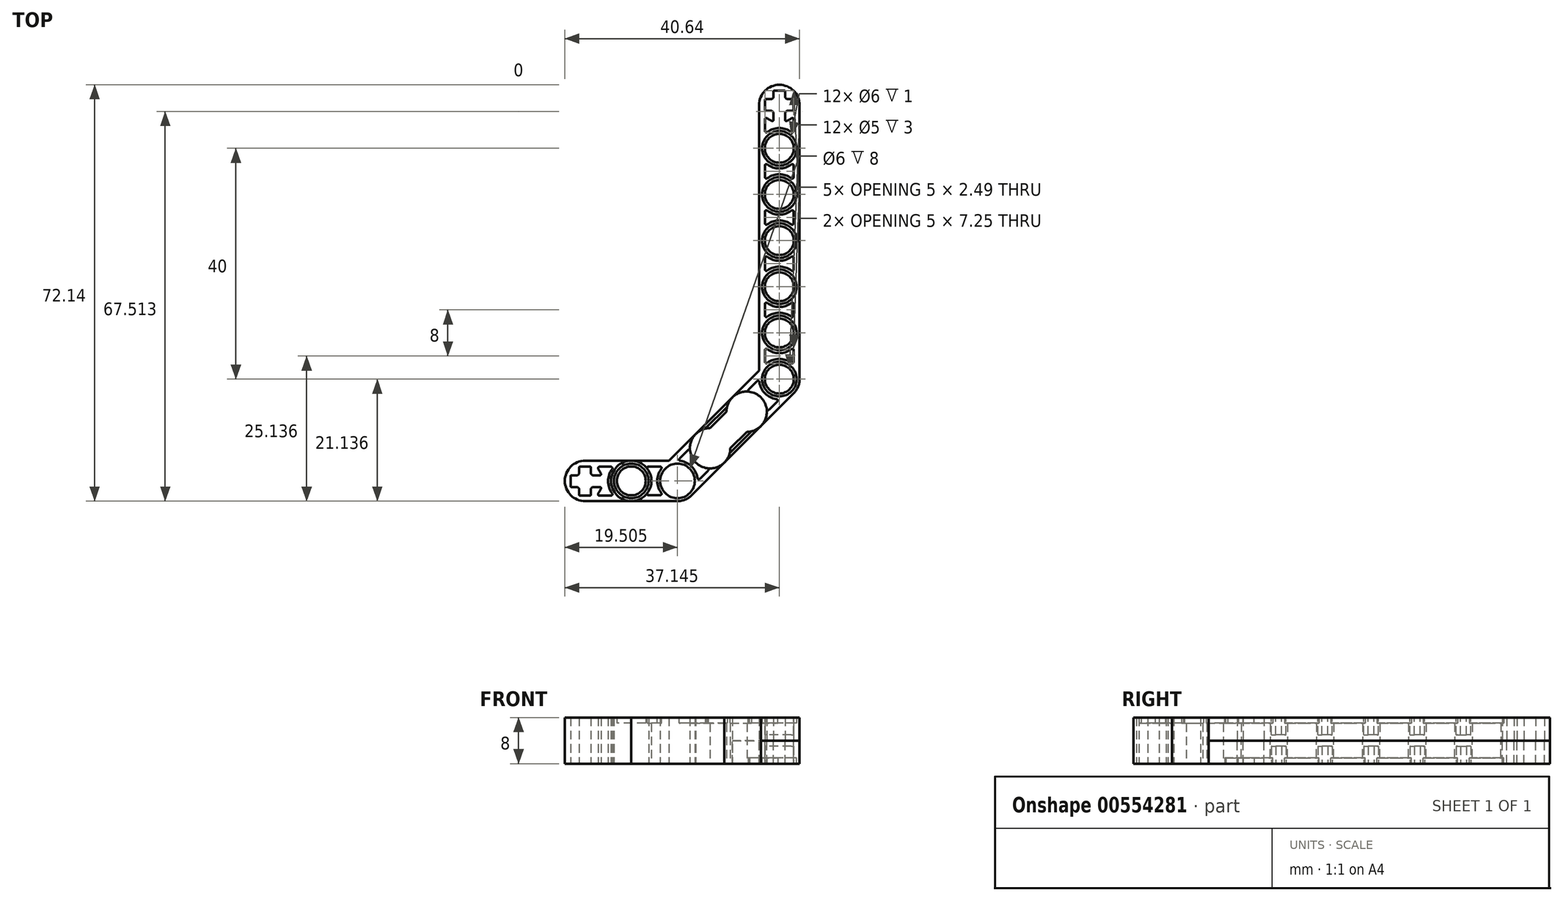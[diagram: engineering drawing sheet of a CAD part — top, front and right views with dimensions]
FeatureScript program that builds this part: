
annotation { "Feature Type Name" : "Feature", "Feature Type Description" : "" }
export const myFeature = defineFeature(function(context is Context, id is Id, definition is map)
    precondition{}
    {
        {
            var Q0;
            Q0=qCreatedBy(makeId("Top.planeOp"),FACE);
            var sketch = newSketch(context, id + "F0", { "sketchPlane" : qUnion([Q0])});
            skArc(sketch, "E0", {"start": v(42.78, 53.86) * mm, "mid": v(39.28, 57.36) * mm, "end": v(35.78, 53.86) * mm});
            skCircle(sketch, "E1", {"center": v(39.28, 6.36) * mm, "radius": 3.5 * mm});
            skLineSegment(sketch, "E2", {"start": v(35.78, 53.86) * mm, "end": v(35.78, 6.36) * mm});
            skLineSegment(sketch, "E3", {"start": v(42.78, 53.86) * mm, "end": v(42.78, 6.36) * mm});
            skCircle(sketch, "E4", {"center": v(39.28, 6.36) * mm, "radius": 2.5 * mm});
            skCircle(sketch, "E5", {"center": v(39.28, 6.36) * mm, "radius": 3 * mm});
            skCircle(sketch, "E6", {"center": v(21.64, -11.28) * mm, "radius": 3.5 * mm});
            skLineSegment(sketch, "E7", {"start": v(21.64, -11.28) * mm, "end": v(5.64, -11.28) * mm});
            skCircle(sketch, "E8", {"center": v(5.64, -11.28) * mm, "radius": 3.5 * mm});
            skLineSegment(sketch, "E9", {"start": v(21.64, -7.78) * mm, "end": v(5.64, -7.78) * mm});
            skLineSegment(sketch, "E10", {"start": v(21.64, -14.78) * mm, "end": v(5.64, -14.78) * mm});
            skLineSegment(sketch, "E11", {"start": v(41.76, 3.88) * mm, "end": v(24.12, -13.76) * mm});
            skLineSegment(sketch, "E12", {"start": v(39.28, 6.36) * mm, "end": v(39.28, 14.36) * mm});
            skLineSegment(sketch, "E13", {"start": v(39.28, 14.36) * mm, "end": v(39.28, 22.36) * mm});
            skLineSegment(sketch, "E14", {"start": v(39.28, 22.36) * mm, "end": v(39.28, 30.36) * mm});
            skLineSegment(sketch, "E15", {"start": v(39.28, 30.36) * mm, "end": v(39.28, 38.36) * mm});
            skLineSegment(sketch, "E16", {"start": v(39.28, 38.36) * mm, "end": v(39.28, 46.36) * mm});
            skCircle(sketch, "E17", {"center": v(39.28, 14.36) * mm, "radius": 2.5 * mm});
            skCircle(sketch, "E18", {"center": v(39.28, 14.36) * mm, "radius": 3 * mm});
            skCircle(sketch, "E19", {"center": v(39.28, 14.36) * mm, "radius": 3.5 * mm});
            skCircle(sketch, "E20", {"center": v(39.28, 22.36) * mm, "radius": 2.5 * mm});
            skCircle(sketch, "E21", {"center": v(39.28, 22.36) * mm, "radius": 3 * mm});
            skCircle(sketch, "E22", {"center": v(39.28, 22.36) * mm, "radius": 3.5 * mm});
            skCircle(sketch, "E23", {"center": v(39.28, 30.36) * mm, "radius": 2.5 * mm});
            skCircle(sketch, "E24", {"center": v(39.28, 30.36) * mm, "radius": 3 * mm});
            skCircle(sketch, "E25", {"center": v(39.28, 30.36) * mm, "radius": 3.5 * mm});
            skCircle(sketch, "E26", {"center": v(39.28, 38.36) * mm, "radius": 2.5 * mm});
            skCircle(sketch, "E27", {"center": v(39.28, 38.36) * mm, "radius": 3 * mm});
            skCircle(sketch, "E28", {"center": v(39.28, 38.36) * mm, "radius": 3.5 * mm});
            skCircle(sketch, "E29", {"center": v(39.28, 46.36) * mm, "radius": 2.5 * mm});
            skCircle(sketch, "E30", {"center": v(39.28, 46.36) * mm, "radius": 3 * mm});
            skArc(sketch, "E31", {"start": v(35.78, 46.36) * mm, "mid": v(39.28, 42.86) * mm, "end": v(42.78, 46.36) * mm});
            skLineSegment(sketch, "E32", {"start": v(39.28, 56.36) * mm, "end": v(38.4, 56.36) * mm});
            skLineSegment(sketch, "E33", {"start": v(39.28, 56.36) * mm, "end": v(40.16, 56.36) * mm});
            skLineSegment(sketch, "E34", {"start": v(41.78, 53.86) * mm, "end": v(41.78, 54.74) * mm});
            skLineSegment(sketch, "E35", {"start": v(41.78, 53.86) * mm, "end": v(41.78, 52.98) * mm});
            skLineSegment(sketch, "E36", {"start": v(36.78, 53.86) * mm, "end": v(36.78, 54.74) * mm});
            skLineSegment(sketch, "E37", {"start": v(36.78, 53.86) * mm, "end": v(36.78, 52.98) * mm});
            skLineSegment(sketch, "E38", {"start": v(36.9, 54.86) * mm, "end": v(37.78, 54.86) * mm});
            skLineSegment(sketch, "E39", {"start": v(38.28, 55.36) * mm, "end": v(38.28, 56.24) * mm});
            skLineSegment(sketch, "E40", {"start": v(40.28, 56.24) * mm, "end": v(40.28, 55.36) * mm});
            skLineSegment(sketch, "E41", {"start": v(40.78, 54.86) * mm, "end": v(41.66, 54.86) * mm});
            skLineSegment(sketch, "E42", {"start": v(41.66, 52.86) * mm, "end": v(40.78, 52.86) * mm});
            skLineSegment(sketch, "E43", {"start": v(36.9, 52.86) * mm, "end": v(37.78, 52.86) * mm});
            skPoint(sketch, "E44.visualSharp", {"position": v(38.28, 56.36) * mm});
            skArc(sketch, "E44.filletArc", {"start": v(38.4, 56.36) * mm, "mid": v(38.32, 56.32) * mm, "end": v(38.28, 56.24) * mm});
            skPoint(sketch, "E45.visualSharp", {"position": v(40.28, 56.36) * mm});
            skArc(sketch, "E45.filletArc", {"start": v(40.28, 56.24) * mm, "mid": v(40.25, 56.32) * mm, "end": v(40.16, 56.36) * mm});
            skPoint(sketch, "E46.visualSharp", {"position": v(36.78, 54.86) * mm});
            skArc(sketch, "E46.filletArc", {"start": v(36.9, 54.86) * mm, "mid": v(36.82, 54.82) * mm, "end": v(36.78, 54.74) * mm});
            skPoint(sketch, "E47.visualSharp", {"position": v(36.78, 52.86) * mm});
            skArc(sketch, "E47.filletArc", {"start": v(36.78, 52.98) * mm, "mid": v(36.82, 52.9) * mm, "end": v(36.9, 52.86) * mm});
            skPoint(sketch, "E48.visualSharp", {"position": v(41.78, 54.86) * mm});
            skArc(sketch, "E48.filletArc", {"start": v(41.78, 54.74) * mm, "mid": v(41.75, 54.82) * mm, "end": v(41.66, 54.86) * mm});
            skPoint(sketch, "E49.visualSharp", {"position": v(41.78, 52.86) * mm});
            skArc(sketch, "E49.filletArc", {"start": v(41.66, 52.86) * mm, "mid": v(41.75, 52.9) * mm, "end": v(41.78, 52.98) * mm});
            skPoint(sketch, "E50.visualSharp", {"position": v(38.28, 54.86) * mm});
            skArc(sketch, "E50.filletArc", {"start": v(37.78, 54.86) * mm, "mid": v(38.14, 55) * mm, "end": v(38.28, 55.36) * mm});
            skPoint(sketch, "E51.visualSharp", {"position": v(40.28, 54.86) * mm});
            skArc(sketch, "E51.filletArc", {"start": v(40.28, 55.36) * mm, "mid": v(40.43, 55) * mm, "end": v(40.78, 54.86) * mm});
            skLineSegment(sketch, "E52", {"start": v(36.78, 50.1) * mm, "end": v(36.78, 49.36) * mm});
            skLineSegment(sketch, "E53", {"start": v(36.78, 50.1) * mm, "end": v(36.78, 51.35) * mm});
            skLineSegment(sketch, "E54", {"start": v(41.78, 50.04) * mm, "end": v(41.78, 49.36) * mm});
            skLineSegment(sketch, "E55", {"start": v(41.78, 50.04) * mm, "end": v(41.78, 51.35) * mm});
            skArc(sketch, "E56", {"start": v(37.19, 51.55) * mm, "mid": v(37.59, 51.3) * mm, "end": v(38.01, 51.1) * mm});
            skLineSegment(sketch, "E57.trimOffspring", {"start": v(39.28, 49.36) * mm, "end": v(39.28, 6.36) * mm});
            skLineSegment(sketch, "E58", {"start": v(40.28, 52.36) * mm, "end": v(40.28, 51.28) * mm});
            skLineSegment(sketch, "E59", {"start": v(38.28, 52.36) * mm, "end": v(38.28, 51.28) * mm});
            skPoint(sketch, "E60.visualSharp", {"position": v(38.28, 52.86) * mm});
            skArc(sketch, "E60.filletArc", {"start": v(38.28, 52.36) * mm, "mid": v(38.14, 52.7) * mm, "end": v(37.78, 52.86) * mm});
            skPoint(sketch, "E61.visualSharp", {"position": v(40.28, 52.86) * mm});
            skArc(sketch, "E61.filletArc", {"start": v(40.78, 52.86) * mm, "mid": v(40.43, 52.7) * mm, "end": v(40.28, 52.36) * mm});
            skArc(sketch, "E62.trimOffspring", {"start": v(40.56, 51.1) * mm, "mid": v(40.98, 51.3) * mm, "end": v(41.38, 51.55) * mm});
            skPoint(sketch, "E63.visualSharp", {"position": v(40.28, 51) * mm});
            skArc(sketch, "E63.filletArc", {"start": v(40.28, 51.28) * mm, "mid": v(40.37, 51.12) * mm, "end": v(40.56, 51.1) * mm});
            skPoint(sketch, "E64.visualSharp", {"position": v(38.28, 51) * mm});
            skArc(sketch, "E64.filletArc", {"start": v(38.01, 51.1) * mm, "mid": v(38.2, 51.12) * mm, "end": v(38.28, 51.28) * mm});
            skPoint(sketch, "E65.visualSharp", {"position": v(36.78, 51.9) * mm});
            skArc(sketch, "E65.filletArc", {"start": v(37.19, 51.55) * mm, "mid": v(36.92, 51.58) * mm, "end": v(36.78, 51.35) * mm});
            skArc(sketch, "E66.trimOffspring", {"start": v(41.38, 49.16) * mm, "mid": v(39.28, 49.86) * mm, "end": v(37.19, 49.16) * mm});
            skPoint(sketch, "E67.visualSharp", {"position": v(36.78, 48.8) * mm});
            skArc(sketch, "E67.filletArc", {"start": v(36.78, 49.36) * mm, "mid": v(36.92, 49.14) * mm, "end": v(37.19, 49.16) * mm});
            skPoint(sketch, "E68.visualSharp", {"position": v(41.78, 48.8) * mm});
            skArc(sketch, "E68.filletArc", {"start": v(41.38, 49.16) * mm, "mid": v(41.64, 49.14) * mm, "end": v(41.78, 49.36) * mm});
            skPoint(sketch, "E69.visualSharp", {"position": v(41.78, 51.9) * mm});
            skArc(sketch, "E69.filletArc", {"start": v(41.78, 51.35) * mm, "mid": v(41.64, 51.58) * mm, "end": v(41.38, 51.55) * mm});
            skLineSegment(sketch, "E70", {"start": v(3.13, -11.33) * mm, "end": v(3.13, -12.21) * mm});
            skLineSegment(sketch, "E71", {"start": v(3.13, -11.33) * mm, "end": v(3.13, -10.45) * mm});
            skLineSegment(sketch, "E72", {"start": v(5.63, -8.83) * mm, "end": v(4.75, -8.83) * mm});
            skLineSegment(sketch, "E73", {"start": v(5.63, -8.83) * mm, "end": v(6.51, -8.83) * mm});
            skLineSegment(sketch, "E74", {"start": v(5.63, -13.83) * mm, "end": v(4.75, -13.83) * mm});
            skLineSegment(sketch, "E75", {"start": v(5.63, -13.83) * mm, "end": v(6.51, -13.83) * mm});
            skLineSegment(sketch, "E76", {"start": v(4.63, -13.71) * mm, "end": v(4.63, -12.83) * mm});
            skLineSegment(sketch, "E77", {"start": v(4.13, -12.33) * mm, "end": v(3.25, -12.33) * mm});
            skLineSegment(sketch, "E78", {"start": v(3.25, -10.33) * mm, "end": v(4.13, -10.33) * mm});
            skLineSegment(sketch, "E79", {"start": v(4.63, -9.83) * mm, "end": v(4.63, -8.95) * mm});
            skLineSegment(sketch, "E80", {"start": v(6.63, -8.95) * mm, "end": v(6.63, -9.83) * mm});
            skLineSegment(sketch, "E81", {"start": v(6.63, -13.71) * mm, "end": v(6.63, -12.83) * mm});
            skPoint(sketch, "E82.visualSharp", {"position": v(3.13, -12.33) * mm});
            skArc(sketch, "E82.filletArc", {"start": v(3.13, -12.21) * mm, "mid": v(3.17, -12.3) * mm, "end": v(3.25, -12.33) * mm});
            skPoint(sketch, "E83.visualSharp", {"position": v(3.13, -10.33) * mm});
            skArc(sketch, "E83.filletArc", {"start": v(3.25, -10.33) * mm, "mid": v(3.17, -10.37) * mm, "end": v(3.13, -10.45) * mm});
            skPoint(sketch, "E84.visualSharp", {"position": v(4.63, -13.83) * mm});
            skArc(sketch, "E84.filletArc", {"start": v(4.63, -13.71) * mm, "mid": v(4.67, -13.8) * mm, "end": v(4.75, -13.83) * mm});
            skPoint(sketch, "E85.visualSharp", {"position": v(6.63, -13.83) * mm});
            skArc(sketch, "E85.filletArc", {"start": v(6.51, -13.83) * mm, "mid": v(6.6, -13.8) * mm, "end": v(6.63, -13.71) * mm});
            skPoint(sketch, "E86.visualSharp", {"position": v(4.63, -8.83) * mm});
            skArc(sketch, "E86.filletArc", {"start": v(4.75, -8.83) * mm, "mid": v(4.67, -8.87) * mm, "end": v(4.63, -8.95) * mm});
            skPoint(sketch, "E87.visualSharp", {"position": v(6.63, -8.83) * mm});
            skArc(sketch, "E87.filletArc", {"start": v(6.63, -8.95) * mm, "mid": v(6.6, -8.87) * mm, "end": v(6.51, -8.83) * mm});
            skPoint(sketch, "E88.visualSharp", {"position": v(4.63, -12.33) * mm});
            skArc(sketch, "E88.filletArc", {"start": v(4.63, -12.83) * mm, "mid": v(4.48, -12.48) * mm, "end": v(4.13, -12.33) * mm});
            skPoint(sketch, "E89.visualSharp", {"position": v(4.63, -10.33) * mm});
            skArc(sketch, "E89.filletArc", {"start": v(4.13, -10.33) * mm, "mid": v(4.48, -10.19) * mm, "end": v(4.63, -9.83) * mm});
            skLineSegment(sketch, "E90", {"start": v(9.39, -13.83) * mm, "end": v(10.13, -13.83) * mm});
            skLineSegment(sketch, "E91", {"start": v(9.39, -13.83) * mm, "end": v(8.14, -13.83) * mm});
            skLineSegment(sketch, "E92", {"start": v(9.45, -8.83) * mm, "end": v(10.13, -8.83) * mm});
            skLineSegment(sketch, "E93", {"start": v(9.45, -8.83) * mm, "end": v(8.14, -8.83) * mm});
            skArc(sketch, "E94", {"start": v(7.93, -13.43) * mm, "mid": v(8.2, -13.03) * mm, "end": v(8.4, -12.6) * mm});
            skLineSegment(sketch, "E95", {"start": v(7.13, -10.33) * mm, "end": v(8.2, -10.33) * mm});
            skLineSegment(sketch, "E96", {"start": v(7.13, -12.33) * mm, "end": v(8.2, -12.33) * mm});
            skPoint(sketch, "E97.visualSharp", {"position": v(6.63, -12.33) * mm});
            skArc(sketch, "E97.filletArc", {"start": v(7.13, -12.33) * mm, "mid": v(6.78, -12.48) * mm, "end": v(6.63, -12.83) * mm});
            skPoint(sketch, "E98.visualSharp", {"position": v(6.63, -10.33) * mm});
            skArc(sketch, "E98.filletArc", {"start": v(6.63, -9.83) * mm, "mid": v(6.78, -10.19) * mm, "end": v(7.13, -10.33) * mm});
            skArc(sketch, "E99.trimOffspring", {"start": v(8.4, -10.06) * mm, "mid": v(8.2, -9.63) * mm, "end": v(7.93, -9.24) * mm});
            skPoint(sketch, "E100.visualSharp", {"position": v(8.49, -10.33) * mm});
            skArc(sketch, "E100.filletArc", {"start": v(8.2, -10.33) * mm, "mid": v(8.37, -10.25) * mm, "end": v(8.4, -10.06) * mm});
            skPoint(sketch, "E101.visualSharp", {"position": v(8.49, -12.33) * mm});
            skArc(sketch, "E101.filletArc", {"start": v(8.4, -12.6) * mm, "mid": v(8.37, -12.42) * mm, "end": v(8.2, -12.33) * mm});
            skPoint(sketch, "E102.visualSharp", {"position": v(7.58, -13.83) * mm});
            skArc(sketch, "E102.filletArc", {"start": v(7.93, -13.43) * mm, "mid": v(7.91, -13.7) * mm, "end": v(8.14, -13.83) * mm});
            skArc(sketch, "E103.trimOffspring", {"start": v(10.33, -9.24) * mm, "mid": v(9.63, -11.33) * mm, "end": v(10.33, -13.43) * mm});
            skPoint(sketch, "E104.visualSharp", {"position": v(10.68, -13.83) * mm});
            skArc(sketch, "E104.filletArc", {"start": v(10.13, -13.83) * mm, "mid": v(10.35, -13.7) * mm, "end": v(10.33, -13.43) * mm});
            skPoint(sketch, "E105.visualSharp", {"position": v(10.68, -8.83) * mm});
            skArc(sketch, "E105.filletArc", {"start": v(10.33, -9.24) * mm, "mid": v(10.35, -8.97) * mm, "end": v(10.13, -8.83) * mm});
            skPoint(sketch, "E106.visualSharp", {"position": v(7.58, -8.83) * mm});
            skArc(sketch, "E106.filletArc", {"start": v(8.14, -8.83) * mm, "mid": v(7.91, -8.97) * mm, "end": v(7.93, -9.24) * mm});
            skLineSegment(sketch, "E107", {"start": v(21.64, -11.28) * mm, "end": v(39.28, 6.36) * mm});
            skLineSegment(sketch, "E108", {"start": v(21.64, -11.28) * mm, "end": v(13.64, -11.28) * mm});
            skCircle(sketch, "E109", {"center": v(13.64, -11.28) * mm, "radius": 3.5 * mm});
            skCircle(sketch, "E110", {"center": v(13.64, -11.28) * mm, "radius": 3 * mm});
            skCircle(sketch, "E111", {"center": v(13.64, -11.28) * mm, "radius": 2.5 * mm});
            skCircle(sketch, "E112", {"center": v(21.64, -11.28) * mm, "radius": 3 * mm});
            skCircle(sketch, "E113", {"center": v(21.64, -11.28) * mm, "radius": 2.5 * mm});
            skLineSegment(sketch, "E114", {"start": v(21.64, -11.28) * mm, "end": v(27.3, -5.63) * mm});
            skCircle(sketch, "E115", {"center": v(27.3, -5.63) * mm, "radius": 3.5 * mm});
            skLineSegment(sketch, "E116", {"start": v(39.28, 6.36) * mm, "end": v(33.63, 0.7) * mm});
            skCircle(sketch, "E117", {"center": v(33.63, 0.7) * mm, "radius": 3.5 * mm});
            skLineSegment(sketch, "E118", {"start": v(24.83, -3.15) * mm, "end": v(35.78, 7.8) * mm});
            skLineSegment(sketch, "E119", {"start": v(24.83, -3.15) * mm, "end": v(20.2, -7.78) * mm});
            skCircle(sketch, "E120", {"center": v(27.3, -5.63) * mm, "radius": 3 * mm});
            skCircle(sketch, "E121", {"center": v(27.3, -5.63) * mm, "radius": 2.5 * mm});
            skCircle(sketch, "E122", {"center": v(33.63, 0.7) * mm, "radius": 2.5 * mm});
            skLineSegment(sketch, "E123", {"start": v(31.86, 2.47) * mm, "end": v(25.53, -3.86) * mm});
            skLineSegment(sketch, "E124", {"start": v(29.07, -7.4) * mm, "end": v(35.4, -1.07) * mm});
            skLineSegment(sketch, "E125", {"start": v(3.13, -12.33) * mm, "end": v(4.63, -12.33) * mm});
            skSolve(sketch);
        }
        {
            var Q0;
            Q0=makeQuery(id+"F0.imprint","IMPRINT",FACE,{"disambiguationData":[TD([[makeQuery(id+"F0.imprint","IMPRINT",EDGE,{"derivedFrom":sQuery(id+"F0.wireOp",EDGE,"E70")}),-1.0]])]});
            var Q1;
            {var subQ0=sQuery(id+"F0.wireOp",EDGE,"E92");Q1=makeQuery(id+"F0.imprint","IMPRINT",FACE,{"disambiguationData":[TD([[makeQuery(id+"F0.imprint","IMPRINT",EDGE,{"derivedFrom":subQ0}),1.0]])]});}
            var Q2;
            Q2=makeQuery(id+"F0.imprint","IMPRINT",FACE,{"disambiguationData":[TD([[makeQuery(id+"F0.imprint","IMPRINT",EDGE,{"derivedFrom":sQuery(id+"F0.wireOp",EDGE,"E90")}),-1.0]])]});
            var Q3;
            {var subQ0=sQuery(id+"F0.wireOp",EDGE,"E10");var subQ1=sQuery(id+"F0.wireOp",EDGE,"E6");var subQ2=makeQuery(id+"F0.imprint","INTERSECT",VERTEX,{"derivedFrom":[subQ1,subQ0]});Q3=makeQuery(id+"F0.imprint","IMPRINT",FACE,{"disambiguationData":[TD([[makeQuery(id+"F0.imprint","IMPRINT",EDGE,{"disambiguationData":[TD([[subQ2,1.0]])],"derivedFrom":subQ1}),-1.0]])]});}
            var Q4;
            {var subQ1=sQuery(id+"F0.wireOp",EDGE,"E6");var subQ5=sQuery(id+"F0.wireOp",EDGE,"E9");var subQ6=makeQuery(id+"F0.imprint","INTERSECT",VERTEX,{"derivedFrom":[subQ1,subQ5]});Q4=makeQuery(id+"F0.imprint","IMPRINT",FACE,{"disambiguationData":[TD([[makeQuery(id+"F0.imprint","IMPRINT",EDGE,{"disambiguationData":[TD([[subQ6,-1.0]])],"derivedFrom":subQ1}),-1.0]])]});}
            var Q5;
            {var subQ2=sQuery(id+"F0.wireOp",EDGE,"E7");var subQ6=sQuery(id+"F0.wireOp",EDGE,"E110");var subQ7=makeQuery(id+"F0.imprint","INTERSECT",VERTEX,{"derivedFrom":[subQ2,subQ6]});Q5=makeQuery(id+"F0.imprint","IMPRINT",FACE,{"disambiguationData":[TD([[makeQuery(id+"F0.imprint","IMPRINT",EDGE,{"disambiguationData":[TD([[subQ7,-1.0]])],"derivedFrom":subQ2}),-1.0]])]});}
            var Q6;
            {var subQ4=sQuery(id+"F0.wireOp",EDGE,"E7");var subQ6=sQuery(id+"F0.wireOp",EDGE,"E110");var subQ8=makeQuery(id+"F0.imprint","INTERSECT",VERTEX,{"derivedFrom":[subQ4,subQ6]});Q6=makeQuery(id+"F0.imprint","IMPRINT",FACE,{"disambiguationData":[TD([[makeQuery(id+"F0.imprint","IMPRINT",EDGE,{"disambiguationData":[TD([[subQ8,-1.0]])],"derivedFrom":subQ4}),1.0]])]});}
            var Q7;
            {var subQ1=sQuery(id+"F0.wireOp",EDGE,"E6");var subQ7=makeQuery(id+"F0.imprint","INTERSECT",VERTEX,{"derivedFrom":[subQ1,sQuery(id+"F0.wireOp",EDGE,"E9")]});Q7=makeQuery(id+"F0.imprint","IMPRINT",FACE,{"disambiguationData":[TD([[makeQuery(id+"F0.imprint","IMPRINT",EDGE,{"disambiguationData":[TD([[subQ7,1.0]])],"derivedFrom":subQ1}),1.0]])]});}
            var Q8;
            {var subQ0=sQuery(id+"F0.wireOp",EDGE,"E119");Q8=makeQuery(id+"F0.imprint","IMPRINT",FACE,{"disambiguationData":[TD([[makeQuery(id+"F0.imprint","IMPRINT",EDGE,{"derivedFrom":subQ0}),1.0]])]});}
            var Q9;
            {var subQ0=sQuery(id+"F0.wireOp",EDGE,"E6");var subQ8=makeQuery(id+"F0.imprint","INTERSECT",VERTEX,{"derivedFrom":[subQ0,sQuery(id+"F0.wireOp",EDGE,"E10")]});Q9=makeQuery(id+"F0.imprint","IMPRINT",FACE,{"disambiguationData":[TD([[makeQuery(id+"F0.imprint","IMPRINT",EDGE,{"disambiguationData":[TD([[subQ8,1.0]])],"derivedFrom":subQ0}),1.0]])]});}
            var Q10;
            {var subQ0=sQuery(id+"F0.wireOp",EDGE,"E11");var subQ1=sQuery(id+"F0.wireOp",EDGE,"E6");var subQ2=makeQuery(id+"F0.imprint","INTERSECT",VERTEX,{"derivedFrom":[subQ1,subQ0]});Q10=makeQuery(id+"F0.imprint","IMPRINT",FACE,{"disambiguationData":[TD([[makeQuery(id+"F0.imprint","IMPRINT",EDGE,{"disambiguationData":[TD([[subQ2,-1.0]])],"derivedFrom":subQ1}),-1.0]])]});}
            var Q11;
            {var subQ0=sQuery(id+"F0.wireOp",EDGE,"E115");var subQ5=sQuery(id+"F0.wireOp",EDGE,"E114");var subQ8=makeQuery(id+"F0.imprint","INTERSECT",VERTEX,{"derivedFrom":[subQ5,subQ0]});Q11=makeQuery(id+"F0.imprint","IMPRINT",FACE,{"disambiguationData":[TD([[makeQuery(id+"F0.imprint","IMPRINT",EDGE,{"disambiguationData":[TD([[subQ8,-1.0]])],"derivedFrom":subQ5}),-1.0]])]});}
            var Q12;
            {var subQ0=sQuery(id+"F0.wireOp",EDGE,"E115");var subQ5=sQuery(id+"F0.wireOp",EDGE,"E114");var subQ8=makeQuery(id+"F0.imprint","INTERSECT",VERTEX,{"derivedFrom":[subQ5,subQ0]});Q12=makeQuery(id+"F0.imprint","IMPRINT",FACE,{"disambiguationData":[TD([[makeQuery(id+"F0.imprint","IMPRINT",EDGE,{"disambiguationData":[TD([[subQ8,-1.0]])],"derivedFrom":subQ5}),1.0]])]});}
            var Q13;
            {var subQ0=sQuery(id+"F0.wireOp",EDGE,"E118");var subQ5=sQuery(id+"F0.wireOp",EDGE,"E117");var subQ6=makeQuery(id+"F0.imprint","INTERSECT",VERTEX,{"derivedFrom":[subQ5,subQ0]});Q13=makeQuery(id+"F0.imprint","IMPRINT",FACE,{"disambiguationData":[TD([[makeQuery(id+"F0.imprint","IMPRINT",EDGE,{"disambiguationData":[TD([[subQ6,-1.0]])],"derivedFrom":subQ5}),-1.0]])]});}
            var Q14;
            {var subQ0=sQuery(id+"F0.wireOp",EDGE,"E120");var subQ1=sQuery(id+"F0.wireOp",EDGE,"E114");var subQ2=makeQuery(id+"F0.imprint","INTERSECT",VERTEX,{"derivedFrom":[subQ1,subQ0]});Q14=makeQuery(id+"F0.imprint","IMPRINT",FACE,{"disambiguationData":[TD([[makeQuery(id+"F0.imprint","IMPRINT",EDGE,{"disambiguationData":[TD([[subQ2,-1.0]])],"derivedFrom":subQ1}),1.0]])]});}
            var Q15;
            {var subQ0=sQuery(id+"F0.wireOp",EDGE,"E120");var subQ1=sQuery(id+"F0.wireOp",EDGE,"E114");var subQ2=makeQuery(id+"F0.imprint","INTERSECT",VERTEX,{"derivedFrom":[subQ1,subQ0]});Q15=makeQuery(id+"F0.imprint","IMPRINT",FACE,{"disambiguationData":[TD([[makeQuery(id+"F0.imprint","IMPRINT",EDGE,{"disambiguationData":[TD([[subQ2,-1.0]])],"derivedFrom":subQ1}),-1.0]])]});}
            var Q16;
            {var subQ0=sQuery(id+"F0.wireOp",EDGE,"E117");var subQ1=sQuery(id+"F0.wireOp",EDGE,"E11");var subQ2=makeQuery(id+"F0.imprint","INTERSECT",VERTEX,{"derivedFrom":[subQ1,subQ0]});Q16=makeQuery(id+"F0.imprint","IMPRINT",FACE,{"disambiguationData":[TD([[makeQuery(id+"F0.imprint","IMPRINT",EDGE,{"disambiguationData":[TD([[subQ2,-1.0]])],"derivedFrom":subQ1}),-1.0]])]});}
            var Q17;
            {var subQ3=sQuery(id+"F0.wireOp",EDGE,"E116");var subQ5=sQuery(id+"F0.wireOp",EDGE,"E117");var subQ6=makeQuery(id+"F0.imprint","INTERSECT",VERTEX,{"derivedFrom":[subQ3,subQ5]});Q17=makeQuery(id+"F0.imprint","IMPRINT",FACE,{"disambiguationData":[TD([[makeQuery(id+"F0.imprint","IMPRINT",EDGE,{"disambiguationData":[TD([[subQ6,-1.0]])],"derivedFrom":subQ3}),1.0]])]});}
            var Q18;
            {var subQ3=sQuery(id+"F0.wireOp",EDGE,"E116");var subQ5=sQuery(id+"F0.wireOp",EDGE,"E117");var subQ8=makeQuery(id+"F0.imprint","INTERSECT",VERTEX,{"derivedFrom":[subQ3,subQ5]});Q18=makeQuery(id+"F0.imprint","IMPRINT",FACE,{"disambiguationData":[TD([[makeQuery(id+"F0.imprint","IMPRINT",EDGE,{"disambiguationData":[TD([[subQ8,-1.0]])],"derivedFrom":subQ3}),-1.0]])]});}
            var Q19;
            {var subQ0=sQuery(id+"F0.wireOp",EDGE,"E11");var subQ1=sQuery(id+"F0.wireOp",EDGE,"E1");var subQ2=makeQuery(id+"F0.imprint","INTERSECT",VERTEX,{"derivedFrom":[subQ1,subQ0]});Q19=makeQuery(id+"F0.imprint","IMPRINT",FACE,{"disambiguationData":[TD([[makeQuery(id+"F0.imprint","IMPRINT",EDGE,{"disambiguationData":[TD([[subQ2,1.0]])],"derivedFrom":subQ1}),-1.0]])]});}
            var Q20;
            {var subQ1=sQuery(id+"F0.wireOp",EDGE,"E1");var subQ5=sQuery(id+"F0.wireOp",EDGE,"E2");var subQ6=makeQuery(id+"F0.imprint","INTERSECT",VERTEX,{"derivedFrom":[subQ1,subQ5]});Q20=makeQuery(id+"F0.imprint","IMPRINT",FACE,{"disambiguationData":[TD([[makeQuery(id+"F0.imprint","IMPRINT",EDGE,{"disambiguationData":[TD([[subQ6,-1.0]])],"derivedFrom":subQ1}),-1.0]])]});}
            var Q21;
            {var subQ5=sQuery(id+"F0.wireOp",EDGE,"E1");var subQ6=makeQuery(id+"F0.imprint","INTERSECT",VERTEX,{"derivedFrom":[subQ5,sQuery(id+"F0.wireOp",EDGE,"E3")]});Q21=makeQuery(id+"F0.imprint","IMPRINT",FACE,{"disambiguationData":[TD([[makeQuery(id+"F0.imprint","IMPRINT",EDGE,{"disambiguationData":[TD([[subQ6,-1.0]])],"derivedFrom":subQ5}),1.0]])]});}
            var Q22;
            {var subQ0=sQuery(id+"F0.wireOp",EDGE,"E3");var subQ1=sQuery(id+"F0.wireOp",EDGE,"E1");var subQ2=makeQuery(id+"F0.imprint","INTERSECT",VERTEX,{"derivedFrom":[subQ1,subQ0]});Q22=makeQuery(id+"F0.imprint","IMPRINT",FACE,{"disambiguationData":[TD([[makeQuery(id+"F0.imprint","IMPRINT",EDGE,{"disambiguationData":[TD([[subQ2,-1.0]])],"derivedFrom":subQ1}),-1.0]])]});}
            var Q23;
            {var subQ0=sQuery(id+"F0.wireOp",EDGE,"E2");var subQ6=sQuery(id+"F0.wireOp",EDGE,"E1");var subQ7=makeQuery(id+"F0.imprint","INTERSECT",VERTEX,{"derivedFrom":[subQ6,subQ0]});Q23=makeQuery(id+"F0.imprint","IMPRINT",FACE,{"disambiguationData":[TD([[makeQuery(id+"F0.imprint","IMPRINT",EDGE,{"disambiguationData":[TD([[subQ7,1.0]])],"derivedFrom":subQ6}),-1.0]])]});}
            var Q24;
            {var subQ5=sQuery(id+"F0.wireOp",EDGE,"E1");var subQ7=makeQuery(id+"F0.imprint","INTERSECT",VERTEX,{"derivedFrom":[subQ5,sQuery(id+"F0.wireOp",EDGE,"E2")]});Q24=makeQuery(id+"F0.imprint","IMPRINT",FACE,{"disambiguationData":[TD([[makeQuery(id+"F0.imprint","IMPRINT",EDGE,{"disambiguationData":[TD([[subQ7,1.0]])],"derivedFrom":subQ5}),1.0]])]});}
            var Q25;
            {var subQ0=sQuery(id+"F0.wireOp",EDGE,"E57.trimOffspring");var subQ1=sQuery(id+"F0.wireOp",EDGE,"E18");var subQ2=makeQuery(id+"F0.imprint","INTERSECT",VERTEX,{"disambiguationData":[OD(0.0)],"derivedFrom":[subQ1,subQ0]});Q25=makeQuery(id+"F0.imprint","IMPRINT",FACE,{"disambiguationData":[TD([[makeQuery(id+"F0.imprint","IMPRINT",EDGE,{"disambiguationData":[TD([[subQ2,1.0]])],"derivedFrom":subQ1}),-1.0]])]});}
            var Q26;
            {var subQ0=sQuery(id+"F0.wireOp",EDGE,"E57.trimOffspring");var subQ1=sQuery(id+"F0.wireOp",EDGE,"E18");var subQ2=makeQuery(id+"F0.imprint","INTERSECT",VERTEX,{"disambiguationData":[OD(0.0)],"derivedFrom":[subQ1,subQ0]});Q26=makeQuery(id+"F0.imprint","IMPRINT",FACE,{"disambiguationData":[TD([[makeQuery(id+"F0.imprint","IMPRINT",EDGE,{"disambiguationData":[TD([[subQ2,-1.0]])],"derivedFrom":subQ1}),-1.0]])]});}
            var Q27;
            {var subQ0=sQuery(id+"F0.wireOp",EDGE,"E22");var subQ1=sQuery(id+"F0.wireOp",EDGE,"E3");var subQ2=makeQuery(id+"F0.imprint","INTERSECT",VERTEX,{"derivedFrom":[subQ1,subQ0]});Q27=makeQuery(id+"F0.imprint","IMPRINT",FACE,{"disambiguationData":[TD([[makeQuery(id+"F0.imprint","IMPRINT",EDGE,{"disambiguationData":[TD([[subQ2,-1.0]])],"derivedFrom":subQ1}),-1.0]])]});}
            var Q28;
            {var subQ0=sQuery(id+"F0.wireOp",EDGE,"E22");var subQ1=sQuery(id+"F0.wireOp",EDGE,"E2");var subQ2=makeQuery(id+"F0.imprint","INTERSECT",VERTEX,{"derivedFrom":[subQ1,subQ0]});Q28=makeQuery(id+"F0.imprint","IMPRINT",FACE,{"disambiguationData":[TD([[makeQuery(id+"F0.imprint","IMPRINT",EDGE,{"disambiguationData":[TD([[subQ2,-1.0]])],"derivedFrom":subQ1}),1.0]])]});}
            var Q29;
            {var subQ0=sQuery(id+"F0.wireOp",EDGE,"E57.trimOffspring");var subQ1=sQuery(id+"F0.wireOp",EDGE,"E21");var subQ2=makeQuery(id+"F0.imprint","INTERSECT",VERTEX,{"disambiguationData":[OD(0.0)],"derivedFrom":[subQ1,subQ0]});Q29=makeQuery(id+"F0.imprint","IMPRINT",FACE,{"disambiguationData":[TD([[makeQuery(id+"F0.imprint","IMPRINT",EDGE,{"disambiguationData":[TD([[subQ2,1.0]])],"derivedFrom":subQ1}),-1.0]])]});}
            var Q30;
            {var subQ0=sQuery(id+"F0.wireOp",EDGE,"E25");var subQ1=sQuery(id+"F0.wireOp",EDGE,"E3");var subQ2=makeQuery(id+"F0.imprint","INTERSECT",VERTEX,{"derivedFrom":[subQ1,subQ0]});Q30=makeQuery(id+"F0.imprint","IMPRINT",FACE,{"disambiguationData":[TD([[makeQuery(id+"F0.imprint","IMPRINT",EDGE,{"disambiguationData":[TD([[subQ2,-1.0]])],"derivedFrom":subQ1}),-1.0]])]});}
            var Q31;
            {var subQ0=sQuery(id+"F0.wireOp",EDGE,"E25");var subQ1=sQuery(id+"F0.wireOp",EDGE,"E2");var subQ2=makeQuery(id+"F0.imprint","INTERSECT",VERTEX,{"derivedFrom":[subQ1,subQ0]});Q31=makeQuery(id+"F0.imprint","IMPRINT",FACE,{"disambiguationData":[TD([[makeQuery(id+"F0.imprint","IMPRINT",EDGE,{"disambiguationData":[TD([[subQ2,-1.0]])],"derivedFrom":subQ1}),1.0]])]});}
            var Q32;
            {var subQ2=sQuery(id+"F0.wireOp",EDGE,"E57.trimOffspring");var subQ4=sQuery(id+"F0.wireOp",EDGE,"E21");var subQ5=makeQuery(id+"F0.imprint","INTERSECT",VERTEX,{"disambiguationData":[OD(0.0)],"derivedFrom":[subQ4,subQ2]});Q32=makeQuery(id+"F0.imprint","IMPRINT",FACE,{"disambiguationData":[TD([[makeQuery(id+"F0.imprint","IMPRINT",EDGE,{"disambiguationData":[TD([[subQ5,-1.0]])],"derivedFrom":subQ4}),-1.0]])]});}
            var Q33;
            {var subQ2=sQuery(id+"F0.wireOp",EDGE,"E57.trimOffspring");var subQ4=sQuery(id+"F0.wireOp",EDGE,"E24");var subQ7=makeQuery(id+"F0.imprint","INTERSECT",VERTEX,{"disambiguationData":[OD(0.0)],"derivedFrom":[subQ4,subQ2]});Q33=makeQuery(id+"F0.imprint","IMPRINT",FACE,{"disambiguationData":[TD([[makeQuery(id+"F0.imprint","IMPRINT",EDGE,{"disambiguationData":[TD([[subQ7,1.0]])],"derivedFrom":subQ4}),-1.0]])]});}
            var Q34;
            {var subQ0=sQuery(id+"F0.wireOp",EDGE,"E28");var subQ1=sQuery(id+"F0.wireOp",EDGE,"E3");var subQ2=makeQuery(id+"F0.imprint","INTERSECT",VERTEX,{"derivedFrom":[subQ1,subQ0]});Q34=makeQuery(id+"F0.imprint","IMPRINT",FACE,{"disambiguationData":[TD([[makeQuery(id+"F0.imprint","IMPRINT",EDGE,{"disambiguationData":[TD([[subQ2,-1.0]])],"derivedFrom":subQ1}),-1.0]])]});}
            var Q35;
            {var subQ0=sQuery(id+"F0.wireOp",EDGE,"E28");var subQ1=sQuery(id+"F0.wireOp",EDGE,"E2");var subQ2=makeQuery(id+"F0.imprint","INTERSECT",VERTEX,{"derivedFrom":[subQ1,subQ0]});Q35=makeQuery(id+"F0.imprint","IMPRINT",FACE,{"disambiguationData":[TD([[makeQuery(id+"F0.imprint","IMPRINT",EDGE,{"disambiguationData":[TD([[subQ2,-1.0]])],"derivedFrom":subQ1}),1.0]])]});}
            var Q36;
            {var subQ0=sQuery(id+"F0.wireOp",EDGE,"E57.trimOffspring");var subQ1=sQuery(id+"F0.wireOp",EDGE,"E24");var subQ2=makeQuery(id+"F0.imprint","INTERSECT",VERTEX,{"disambiguationData":[OD(0.0)],"derivedFrom":[subQ1,subQ0]});Q36=makeQuery(id+"F0.imprint","IMPRINT",FACE,{"disambiguationData":[TD([[makeQuery(id+"F0.imprint","IMPRINT",EDGE,{"disambiguationData":[TD([[subQ2,-1.0]])],"derivedFrom":subQ1}),-1.0]])]});}
            var Q37;
            {var subQ0=sQuery(id+"F0.wireOp",EDGE,"E57.trimOffspring");var subQ1=sQuery(id+"F0.wireOp",EDGE,"E27");var subQ2=makeQuery(id+"F0.imprint","INTERSECT",VERTEX,{"disambiguationData":[OD(0.0)],"derivedFrom":[subQ1,subQ0]});Q37=makeQuery(id+"F0.imprint","IMPRINT",FACE,{"disambiguationData":[TD([[makeQuery(id+"F0.imprint","IMPRINT",EDGE,{"disambiguationData":[TD([[subQ2,-1.0]])],"derivedFrom":subQ1}),-1.0]])]});}
            var Q38;
            {var subQ2=sQuery(id+"F0.wireOp",EDGE,"E57.trimOffspring");var subQ4=sQuery(id+"F0.wireOp",EDGE,"E27");var subQ5=makeQuery(id+"F0.imprint","INTERSECT",VERTEX,{"disambiguationData":[OD(0.0)],"derivedFrom":[subQ4,subQ2]});Q38=makeQuery(id+"F0.imprint","IMPRINT",FACE,{"disambiguationData":[TD([[makeQuery(id+"F0.imprint","IMPRINT",EDGE,{"disambiguationData":[TD([[subQ5,1.0]])],"derivedFrom":subQ4}),-1.0]])]});}
            var Q39;
            {var subQ0=sQuery(id+"F0.wireOp",EDGE,"E31");var subQ1=sQuery(id+"F0.wireOp",EDGE,"E3");var subQ2=makeQuery(id+"F0.imprint","INTERSECT",VERTEX,{"derivedFrom":[subQ1,subQ0]});Q39=makeQuery(id+"F0.imprint","IMPRINT",FACE,{"disambiguationData":[TD([[makeQuery(id+"F0.imprint","IMPRINT",EDGE,{"disambiguationData":[TD([[subQ2,-1.0]])],"derivedFrom":subQ1}),-1.0]])]});}
            var Q40;
            {var subQ0=sQuery(id+"F0.wireOp",EDGE,"E31");var subQ1=sQuery(id+"F0.wireOp",EDGE,"E2");var subQ2=makeQuery(id+"F0.imprint","INTERSECT",VERTEX,{"derivedFrom":[subQ1,subQ0]});Q40=makeQuery(id+"F0.imprint","IMPRINT",FACE,{"disambiguationData":[TD([[makeQuery(id+"F0.imprint","IMPRINT",EDGE,{"disambiguationData":[TD([[subQ2,-1.0]])],"derivedFrom":subQ1}),1.0]])]});}
            var Q41;
            {var subQ0=sQuery(id+"F0.wireOp",EDGE,"E0");Q41=makeQuery(id+"F0.imprint","IMPRINT",FACE,{"disambiguationData":[TD([[makeQuery(id+"F0.imprint","IMPRINT",EDGE,{"derivedFrom":subQ0}),1.0]])]});}
            extrude(context, id + "F1", {"entities" : qUnion([Q0, Q1, Q2, Q3, Q4, Q5, Q6, Q7, Q8, Q9, Q10, Q11, Q12, Q13, Q14, Q15, Q16, Q17, Q18, Q19, Q20, Q21, Q22, Q23, Q24, Q25, Q26, Q27, Q28, Q29, Q30, Q31, Q32, Q33, Q34, Q35, Q36, Q37, Q38, Q39, Q40, Q41]), "depth" : 8 * mm, "offsetDistance" : 25 * mm});
        }
        {
            var Q0;
            Q0=makeQuery(id+"F1.opExtrude","CAP_FACE",FACE,{"disambiguationData":[OSD([sQuery(id+"F0.wireOp",EDGE,"E0"),sQuery(id+"F0.wireOp",EDGE,"E1"),sQuery(id+"F0.wireOp",EDGE,"E2"),sQuery(id+"F0.wireOp",EDGE,"E3"),sQuery(id+"F0.wireOp",EDGE,"E5"),sQuery(id+"F0.wireOp",EDGE,"E6"),sQuery(id+"F0.wireOp",EDGE,"E8"),sQuery(id+"F0.wireOp",EDGE,"E9"),sQuery(id+"F0.wireOp",EDGE,"E10"),sQuery(id+"F0.wireOp",EDGE,"E11"),sQuery(id+"F0.wireOp",EDGE,"E18"),sQuery(id+"F0.wireOp",EDGE,"E21"),sQuery(id+"F0.wireOp",EDGE,"E24"),sQuery(id+"F0.wireOp",EDGE,"E27"),sQuery(id+"F0.wireOp",EDGE,"E30"),sQuery(id+"F0.wireOp",EDGE,"E32"),sQuery(id+"F0.wireOp",EDGE,"E33"),sQuery(id+"F0.wireOp",EDGE,"E34"),sQuery(id+"F0.wireOp",EDGE,"E35"),sQuery(id+"F0.wireOp",EDGE,"E36"),sQuery(id+"F0.wireOp",EDGE,"E37"),sQuery(id+"F0.wireOp",EDGE,"E38"),sQuery(id+"F0.wireOp",EDGE,"E39"),sQuery(id+"F0.wireOp",EDGE,"E40"),sQuery(id+"F0.wireOp",EDGE,"E41"),sQuery(id+"F0.wireOp",EDGE,"E42"),sQuery(id+"F0.wireOp",EDGE,"E43"),sQuery(id+"F0.wireOp",EDGE,"E44.filletArc"),sQuery(id+"F0.wireOp",EDGE,"E45.filletArc"),sQuery(id+"F0.wireOp",EDGE,"E46.filletArc"),sQuery(id+"F0.wireOp",EDGE,"E47.filletArc"),sQuery(id+"F0.wireOp",EDGE,"E48.filletArc"),sQuery(id+"F0.wireOp",EDGE,"E49.filletArc"),sQuery(id+"F0.wireOp",EDGE,"E50.filletArc"),sQuery(id+"F0.wireOp",EDGE,"E51.filletArc"),sQuery(id+"F0.wireOp",EDGE,"E52"),sQuery(id+"F0.wireOp",EDGE,"E53"),sQuery(id+"F0.wireOp",EDGE,"E54"),sQuery(id+"F0.wireOp",EDGE,"E55"),sQuery(id+"F0.wireOp",EDGE,"E56"),sQuery(id+"F0.wireOp",EDGE,"E58"),sQuery(id+"F0.wireOp",EDGE,"E59"),sQuery(id+"F0.wireOp",EDGE,"E60.filletArc"),sQuery(id+"F0.wireOp",EDGE,"E61.filletArc"),sQuery(id+"F0.wireOp",EDGE,"E62.trimOffspring"),sQuery(id+"F0.wireOp",EDGE,"E63.filletArc"),sQuery(id+"F0.wireOp",EDGE,"E64.filletArc"),sQuery(id+"F0.wireOp",EDGE,"E65.filletArc"),sQuery(id+"F0.wireOp",EDGE,"E66.trimOffspring"),sQuery(id+"F0.wireOp",EDGE,"E67.filletArc"),sQuery(id+"F0.wireOp",EDGE,"E68.filletArc"),sQuery(id+"F0.wireOp",EDGE,"E69.filletArc"),sQuery(id+"F0.wireOp",EDGE,"E70"),sQuery(id+"F0.wireOp",EDGE,"E71"),sQuery(id+"F0.wireOp",EDGE,"E72"),sQuery(id+"F0.wireOp",EDGE,"E73"),sQuery(id+"F0.wireOp",EDGE,"E74"),sQuery(id+"F0.wireOp",EDGE,"E75"),sQuery(id+"F0.wireOp",EDGE,"E76"),sQuery(id+"F0.wireOp",EDGE,"E77"),sQuery(id+"F0.wireOp",EDGE,"E78"),sQuery(id+"F0.wireOp",EDGE,"E79"),sQuery(id+"F0.wireOp",EDGE,"E80"),sQuery(id+"F0.wireOp",EDGE,"E81"),sQuery(id+"F0.wireOp",EDGE,"E82.filletArc"),sQuery(id+"F0.wireOp",EDGE,"E83.filletArc"),sQuery(id+"F0.wireOp",EDGE,"E84.filletArc"),sQuery(id+"F0.wireOp",EDGE,"E85.filletArc"),sQuery(id+"F0.wireOp",EDGE,"E86.filletArc"),sQuery(id+"F0.wireOp",EDGE,"E87.filletArc"),sQuery(id+"F0.wireOp",EDGE,"E88.filletArc"),sQuery(id+"F0.wireOp",EDGE,"E89.filletArc"),sQuery(id+"F0.wireOp",EDGE,"E90"),sQuery(id+"F0.wireOp",EDGE,"E91"),sQuery(id+"F0.wireOp",EDGE,"E92"),sQuery(id+"F0.wireOp",EDGE,"E93"),sQuery(id+"F0.wireOp",EDGE,"E94"),sQuery(id+"F0.wireOp",EDGE,"E95"),sQuery(id+"F0.wireOp",EDGE,"E96"),sQuery(id+"F0.wireOp",EDGE,"E97.filletArc"),sQuery(id+"F0.wireOp",EDGE,"E98.filletArc"),sQuery(id+"F0.wireOp",EDGE,"E99.trimOffspring"),sQuery(id+"F0.wireOp",EDGE,"E100.filletArc"),sQuery(id+"F0.wireOp",EDGE,"E101.filletArc"),sQuery(id+"F0.wireOp",EDGE,"E102.filletArc"),sQuery(id+"F0.wireOp",EDGE,"E103.trimOffspring"),sQuery(id+"F0.wireOp",EDGE,"E104.filletArc"),sQuery(id+"F0.wireOp",EDGE,"E105.filletArc"),sQuery(id+"F0.wireOp",EDGE,"E106.filletArc"),sQuery(id+"F0.wireOp",EDGE,"E110"),sQuery(id+"F0.wireOp",EDGE,"E112"),sQuery(id+"F0.wireOp",EDGE,"E118"),sQuery(id+"F0.wireOp",EDGE,"E119"),sQuery(id+"F0.wireOp",EDGE,"E121"),sQuery(id+"F0.wireOp",EDGE,"E122"),sQuery(id+"F0.wireOp",EDGE,"E123"),sQuery(id+"F0.wireOp",EDGE,"E124")])],"isStart":false});
            var sketch = newSketch(context, id + "F2", { "sketchPlane" : qUnion([Q0])});
            skArc(sketch, "E126", {"start": v(37.19, 43.55) * mm, "mid": v(39.28, 42.86) * mm, "end": v(41.38, 43.55) * mm});
            skArc(sketch, "E127", {"start": v(41.38, 41.16) * mm, "mid": v(39.28, 41.86) * mm, "end": v(37.19, 41.16) * mm});
            skLineSegment(sketch, "E128", {"start": v(36.78, 42.33) * mm, "end": v(36.78, 41.36) * mm});
            skLineSegment(sketch, "E129", {"start": v(36.78, 42.33) * mm, "end": v(36.78, 43.35) * mm});
            skLineSegment(sketch, "E130", {"start": v(41.78, 42.42) * mm, "end": v(41.78, 41.36) * mm});
            skLineSegment(sketch, "E131", {"start": v(41.78, 42.42) * mm, "end": v(41.78, 43.35) * mm});
            skPoint(sketch, "E132.visualSharp", {"position": v(36.78, 40.8) * mm});
            skArc(sketch, "E132.filletArc", {"start": v(36.78, 41.36) * mm, "mid": v(36.92, 41.14) * mm, "end": v(37.19, 41.16) * mm});
            skPoint(sketch, "E133.visualSharp", {"position": v(36.78, 43.9) * mm});
            skArc(sketch, "E133.filletArc", {"start": v(37.19, 43.55) * mm, "mid": v(36.92, 43.58) * mm, "end": v(36.78, 43.35) * mm});
            skPoint(sketch, "E134.visualSharp", {"position": v(41.78, 43.9) * mm});
            skArc(sketch, "E134.filletArc", {"start": v(41.78, 43.35) * mm, "mid": v(41.64, 43.58) * mm, "end": v(41.38, 43.55) * mm});
            skPoint(sketch, "E135.visualSharp", {"position": v(41.78, 40.8) * mm});
            skArc(sketch, "E135.filletArc", {"start": v(41.38, 41.16) * mm, "mid": v(41.64, 41.14) * mm, "end": v(41.78, 41.36) * mm});
            skArc(sketch, "E136.0.1.0", {"start": v(41.38, 33.16) * mm, "mid": v(39.28, 33.86) * mm, "end": v(37.19, 33.16) * mm});
            skLineSegment(sketch, "E136.0.1.1", {"start": v(36.78, 34.33) * mm, "end": v(36.78, 33.36) * mm});
            skArc(sketch, "E136.0.1.2", {"start": v(36.78, 33.36) * mm, "mid": v(36.92, 33.14) * mm, "end": v(37.19, 33.16) * mm});
            skLineSegment(sketch, "E136.0.1.3", {"start": v(36.78, 34.33) * mm, "end": v(36.78, 35.35) * mm});
            skArc(sketch, "E136.0.1.4", {"start": v(37.19, 35.55) * mm, "mid": v(36.92, 35.58) * mm, "end": v(36.78, 35.35) * mm});
            skArc(sketch, "E136.0.1.5", {"start": v(37.19, 35.55) * mm, "mid": v(39.28, 34.86) * mm, "end": v(41.38, 35.55) * mm});
            skLineSegment(sketch, "E136.0.1.6", {"start": v(41.78, 34.42) * mm, "end": v(41.78, 33.36) * mm});
            skArc(sketch, "E136.0.1.7", {"start": v(41.38, 33.16) * mm, "mid": v(41.64, 33.14) * mm, "end": v(41.78, 33.36) * mm});
            skLineSegment(sketch, "E136.0.1.8", {"start": v(41.78, 34.42) * mm, "end": v(41.78, 35.35) * mm});
            skArc(sketch, "E136.0.1.9", {"start": v(41.78, 35.35) * mm, "mid": v(41.64, 35.58) * mm, "end": v(41.38, 35.55) * mm});
            skArc(sketch, "E136.0.2.0", {"start": v(41.38, 25.16) * mm, "mid": v(39.28, 25.86) * mm, "end": v(37.19, 25.16) * mm});
            skLineSegment(sketch, "E136.0.2.1", {"start": v(36.78, 26.33) * mm, "end": v(36.78, 25.36) * mm});
            skArc(sketch, "E136.0.2.2", {"start": v(36.78, 25.36) * mm, "mid": v(36.92, 25.14) * mm, "end": v(37.19, 25.16) * mm});
            skLineSegment(sketch, "E136.0.2.3", {"start": v(36.78, 26.33) * mm, "end": v(36.78, 27.35) * mm});
            skArc(sketch, "E136.0.2.4", {"start": v(37.19, 27.55) * mm, "mid": v(36.92, 27.58) * mm, "end": v(36.78, 27.35) * mm});
            skArc(sketch, "E136.0.2.5", {"start": v(37.19, 27.55) * mm, "mid": v(39.28, 26.86) * mm, "end": v(41.38, 27.55) * mm});
            skLineSegment(sketch, "E136.0.2.6", {"start": v(41.78, 26.42) * mm, "end": v(41.78, 25.36) * mm});
            skArc(sketch, "E136.0.2.7", {"start": v(41.38, 25.16) * mm, "mid": v(41.64, 25.14) * mm, "end": v(41.78, 25.36) * mm});
            skLineSegment(sketch, "E136.0.2.8", {"start": v(41.78, 26.42) * mm, "end": v(41.78, 27.35) * mm});
            skArc(sketch, "E136.0.2.9", {"start": v(41.78, 27.35) * mm, "mid": v(41.64, 27.58) * mm, "end": v(41.38, 27.55) * mm});
            skArc(sketch, "E136.0.3.0", {"start": v(41.38, 17.16) * mm, "mid": v(39.28, 17.86) * mm, "end": v(37.19, 17.16) * mm});
            skLineSegment(sketch, "E136.0.3.1", {"start": v(36.78, 18.33) * mm, "end": v(36.78, 17.36) * mm});
            skArc(sketch, "E136.0.3.2", {"start": v(36.78, 17.36) * mm, "mid": v(36.92, 17.14) * mm, "end": v(37.19, 17.16) * mm});
            skLineSegment(sketch, "E136.0.3.3", {"start": v(36.78, 18.33) * mm, "end": v(36.78, 19.35) * mm});
            skArc(sketch, "E136.0.3.4", {"start": v(37.19, 19.55) * mm, "mid": v(36.92, 19.58) * mm, "end": v(36.78, 19.35) * mm});
            skArc(sketch, "E136.0.3.5", {"start": v(37.19, 19.55) * mm, "mid": v(39.28, 18.86) * mm, "end": v(41.38, 19.55) * mm});
            skLineSegment(sketch, "E136.0.3.6", {"start": v(41.78, 18.42) * mm, "end": v(41.78, 17.36) * mm});
            skArc(sketch, "E136.0.3.7", {"start": v(41.38, 17.16) * mm, "mid": v(41.64, 17.14) * mm, "end": v(41.78, 17.36) * mm});
            skLineSegment(sketch, "E136.0.3.8", {"start": v(41.78, 18.42) * mm, "end": v(41.78, 19.35) * mm});
            skArc(sketch, "E136.0.3.9", {"start": v(41.78, 19.35) * mm, "mid": v(41.64, 19.58) * mm, "end": v(41.38, 19.55) * mm});
            skArc(sketch, "E136.0.4.0", {"start": v(41.38, 9.16) * mm, "mid": v(39.28, 9.86) * mm, "end": v(37.19, 9.16) * mm});
            skLineSegment(sketch, "E136.0.4.1", {"start": v(36.78, 10.33) * mm, "end": v(36.78, 9.36) * mm});
            skArc(sketch, "E136.0.4.2", {"start": v(36.78, 9.36) * mm, "mid": v(36.92, 9.14) * mm, "end": v(37.19, 9.16) * mm});
            skLineSegment(sketch, "E136.0.4.3", {"start": v(36.78, 10.33) * mm, "end": v(36.78, 11.35) * mm});
            skArc(sketch, "E136.0.4.4", {"start": v(37.19, 11.55) * mm, "mid": v(36.92, 11.58) * mm, "end": v(36.78, 11.35) * mm});
            skArc(sketch, "E136.0.4.5", {"start": v(37.19, 11.55) * mm, "mid": v(39.28, 10.86) * mm, "end": v(41.38, 11.55) * mm});
            skLineSegment(sketch, "E136.0.4.6", {"start": v(41.78, 10.42) * mm, "end": v(41.78, 9.36) * mm});
            skArc(sketch, "E136.0.4.7", {"start": v(41.38, 9.16) * mm, "mid": v(41.64, 9.14) * mm, "end": v(41.78, 9.36) * mm});
            skLineSegment(sketch, "E136.0.4.8", {"start": v(41.78, 10.42) * mm, "end": v(41.78, 11.35) * mm});
            skArc(sketch, "E136.0.4.9", {"start": v(41.78, 11.35) * mm, "mid": v(41.64, 11.58) * mm, "end": v(41.38, 11.55) * mm});
            skLineSegment(sketch, "E136.direction1", {"start": v(39.28, 38.36) * mm, "end": v(64.28, 38.36) * mm, "construction": true});
            skLineSegment(sketch, "E136.direction2", {"start": v(39.28, 38.36) * mm, "end": v(39.28, 30.36) * mm, "construction": true});
            skSolve(sketch);
        }
        {
            var Q0;
            Q0 = qSketchRegion(id + "F2", true);
            extrude(context, id + "F3", {"entities" : qUnion([Q0]), "operationType" : NewBodyOperationType.REMOVE, "oppositeDirection" : true, "depth" : 3 * mm, "offsetDistance" : 25 * mm});
        }
        {
            var Q0;
            {var subQ0=sQuery(id+"F0.wireOp",EDGE,"E57.trimOffspring");var subQ1=sQuery(id+"F0.wireOp",EDGE,"E29");var subQ2=makeQuery(id+"F0.imprint","INTERSECT",VERTEX,{"disambiguationData":[OD(0.0)],"derivedFrom":[subQ1,subQ0]});Q0=makeQuery(id+"F0.imprint","IMPRINT",FACE,{"disambiguationData":[TD([[makeQuery(id+"F0.imprint","IMPRINT",EDGE,{"disambiguationData":[TD([[subQ2,-1.0]])],"derivedFrom":subQ1}),-1.0]])]});}
            var Q1;
            {var subQ0=sQuery(id+"F0.wireOp",EDGE,"E57.trimOffspring");var subQ1=sQuery(id+"F0.wireOp",EDGE,"E29");var subQ2=makeQuery(id+"F0.imprint","INTERSECT",VERTEX,{"disambiguationData":[OD(0.0)],"derivedFrom":[subQ1,subQ0]});Q1=makeQuery(id+"F0.imprint","IMPRINT",FACE,{"disambiguationData":[TD([[makeQuery(id+"F0.imprint","IMPRINT",EDGE,{"disambiguationData":[TD([[subQ2,1.0]])],"derivedFrom":subQ1}),-1.0]])]});}
            var Q2;
            {var subQ0=sQuery(id+"F0.wireOp",EDGE,"E57.trimOffspring");var subQ1=sQuery(id+"F0.wireOp",EDGE,"E26");var subQ2=makeQuery(id+"F0.imprint","INTERSECT",VERTEX,{"disambiguationData":[OD(0.0)],"derivedFrom":[subQ1,subQ0]});Q2=makeQuery(id+"F0.imprint","IMPRINT",FACE,{"disambiguationData":[TD([[makeQuery(id+"F0.imprint","IMPRINT",EDGE,{"disambiguationData":[TD([[subQ2,-1.0]])],"derivedFrom":subQ1}),-1.0]])]});}
            var Q3;
            {var subQ0=sQuery(id+"F0.wireOp",EDGE,"E57.trimOffspring");var subQ1=sQuery(id+"F0.wireOp",EDGE,"E26");var subQ2=makeQuery(id+"F0.imprint","INTERSECT",VERTEX,{"disambiguationData":[OD(0.0)],"derivedFrom":[subQ1,subQ0]});Q3=makeQuery(id+"F0.imprint","IMPRINT",FACE,{"disambiguationData":[TD([[makeQuery(id+"F0.imprint","IMPRINT",EDGE,{"disambiguationData":[TD([[subQ2,1.0]])],"derivedFrom":subQ1}),-1.0]])]});}
            var Q4;
            {var subQ0=sQuery(id+"F0.wireOp",EDGE,"E57.trimOffspring");var subQ1=sQuery(id+"F0.wireOp",EDGE,"E23");var subQ2=makeQuery(id+"F0.imprint","INTERSECT",VERTEX,{"disambiguationData":[OD(0.0)],"derivedFrom":[subQ1,subQ0]});Q4=makeQuery(id+"F0.imprint","IMPRINT",FACE,{"disambiguationData":[TD([[makeQuery(id+"F0.imprint","IMPRINT",EDGE,{"disambiguationData":[TD([[subQ2,-1.0]])],"derivedFrom":subQ1}),-1.0]])]});}
            var Q5;
            {var subQ0=sQuery(id+"F0.wireOp",EDGE,"E57.trimOffspring");var subQ1=sQuery(id+"F0.wireOp",EDGE,"E23");var subQ2=makeQuery(id+"F0.imprint","INTERSECT",VERTEX,{"disambiguationData":[OD(0.0)],"derivedFrom":[subQ1,subQ0]});Q5=makeQuery(id+"F0.imprint","IMPRINT",FACE,{"disambiguationData":[TD([[makeQuery(id+"F0.imprint","IMPRINT",EDGE,{"disambiguationData":[TD([[subQ2,1.0]])],"derivedFrom":subQ1}),-1.0]])]});}
            var Q6;
            {var subQ0=sQuery(id+"F0.wireOp",EDGE,"E57.trimOffspring");var subQ1=sQuery(id+"F0.wireOp",EDGE,"E20");var subQ2=makeQuery(id+"F0.imprint","INTERSECT",VERTEX,{"disambiguationData":[OD(0.0)],"derivedFrom":[subQ1,subQ0]});Q6=makeQuery(id+"F0.imprint","IMPRINT",FACE,{"disambiguationData":[TD([[makeQuery(id+"F0.imprint","IMPRINT",EDGE,{"disambiguationData":[TD([[subQ2,-1.0]])],"derivedFrom":subQ1}),-1.0]])]});}
            var Q7;
            {var subQ0=sQuery(id+"F0.wireOp",EDGE,"E57.trimOffspring");var subQ1=sQuery(id+"F0.wireOp",EDGE,"E20");var subQ2=makeQuery(id+"F0.imprint","INTERSECT",VERTEX,{"disambiguationData":[OD(0.0)],"derivedFrom":[subQ1,subQ0]});Q7=makeQuery(id+"F0.imprint","IMPRINT",FACE,{"disambiguationData":[TD([[makeQuery(id+"F0.imprint","IMPRINT",EDGE,{"disambiguationData":[TD([[subQ2,1.0]])],"derivedFrom":subQ1}),-1.0]])]});}
            var Q8;
            {var subQ0=sQuery(id+"F0.wireOp",EDGE,"E57.trimOffspring");var subQ1=sQuery(id+"F0.wireOp",EDGE,"E17");var subQ2=makeQuery(id+"F0.imprint","INTERSECT",VERTEX,{"disambiguationData":[OD(0.0)],"derivedFrom":[subQ1,subQ0]});Q8=makeQuery(id+"F0.imprint","IMPRINT",FACE,{"disambiguationData":[TD([[makeQuery(id+"F0.imprint","IMPRINT",EDGE,{"disambiguationData":[TD([[subQ2,-1.0]])],"derivedFrom":subQ1}),-1.0]])]});}
            var Q9;
            {var subQ0=sQuery(id+"F0.wireOp",EDGE,"E57.trimOffspring");var subQ1=sQuery(id+"F0.wireOp",EDGE,"E17");var subQ2=makeQuery(id+"F0.imprint","INTERSECT",VERTEX,{"disambiguationData":[OD(0.0)],"derivedFrom":[subQ1,subQ0]});Q9=makeQuery(id+"F0.imprint","IMPRINT",FACE,{"disambiguationData":[TD([[makeQuery(id+"F0.imprint","IMPRINT",EDGE,{"disambiguationData":[TD([[subQ2,1.0]])],"derivedFrom":subQ1}),-1.0]])]});}
            var Q10;
            {var subQ0=sQuery(id+"F0.wireOp",EDGE,"E57.trimOffspring");var subQ1=sQuery(id+"F0.wireOp",EDGE,"E4");var subQ2=makeQuery(id+"F0.imprint","INTERSECT",VERTEX,{"derivedFrom":[subQ1,subQ0]});Q10=makeQuery(id+"F0.imprint","IMPRINT",FACE,{"disambiguationData":[TD([[makeQuery(id+"F0.imprint","IMPRINT",EDGE,{"disambiguationData":[TD([[subQ2,-1.0]])],"derivedFrom":subQ1}),-1.0]])]});}
            var Q11;
            {var subQ0=sQuery(id+"F0.wireOp",EDGE,"E57.trimOffspring");var subQ1=sQuery(id+"F0.wireOp",EDGE,"E4");var subQ2=makeQuery(id+"F0.imprint","INTERSECT",VERTEX,{"derivedFrom":[subQ1,subQ0]});Q11=makeQuery(id+"F0.imprint","IMPRINT",FACE,{"disambiguationData":[TD([[makeQuery(id+"F0.imprint","IMPRINT",EDGE,{"disambiguationData":[TD([[subQ2,1.0]])],"derivedFrom":subQ1}),-1.0]])]});}
            var Q12;
            {var subQ0=sQuery(id+"F0.wireOp",EDGE,"E113");var subQ1=sQuery(id+"F0.wireOp",EDGE,"E108");var subQ2=makeQuery(id+"F0.imprint","INTERSECT",VERTEX,{"derivedFrom":[subQ1,subQ0]});Q12=makeQuery(id+"F0.imprint","IMPRINT",FACE,{"disambiguationData":[TD([[makeQuery(id+"F0.imprint","IMPRINT",EDGE,{"disambiguationData":[TD([[subQ2,-1.0]])],"derivedFrom":subQ1}),-1.0]])]});}
            var Q13;
            {var subQ0=sQuery(id+"F0.wireOp",EDGE,"E113");var subQ1=sQuery(id+"F0.wireOp",EDGE,"E108");var subQ2=makeQuery(id+"F0.imprint","INTERSECT",VERTEX,{"derivedFrom":[subQ1,subQ0]});Q13=makeQuery(id+"F0.imprint","IMPRINT",FACE,{"disambiguationData":[TD([[makeQuery(id+"F0.imprint","IMPRINT",EDGE,{"disambiguationData":[TD([[subQ2,-1.0]])],"derivedFrom":subQ1}),1.0]])]});}
            var Q14;
            {var subQ0=sQuery(id+"F0.wireOp",EDGE,"E111");var subQ1=sQuery(id+"F0.wireOp",EDGE,"E7");var subQ2=makeQuery(id+"F0.imprint","INTERSECT",VERTEX,{"derivedFrom":[subQ1,subQ0]});Q14=makeQuery(id+"F0.imprint","IMPRINT",FACE,{"disambiguationData":[TD([[makeQuery(id+"F0.imprint","IMPRINT",EDGE,{"disambiguationData":[TD([[subQ2,-1.0]])],"derivedFrom":subQ1}),-1.0]])]});}
            var Q15;
            {var subQ0=sQuery(id+"F0.wireOp",EDGE,"E111");var subQ1=sQuery(id+"F0.wireOp",EDGE,"E7");var subQ2=makeQuery(id+"F0.imprint","INTERSECT",VERTEX,{"derivedFrom":[subQ1,subQ0]});Q15=makeQuery(id+"F0.imprint","IMPRINT",FACE,{"disambiguationData":[TD([[makeQuery(id+"F0.imprint","IMPRINT",EDGE,{"disambiguationData":[TD([[subQ2,-1.0]])],"derivedFrom":subQ1}),1.0]])]});}
            extrude(context, id + "F4", {"entities" : qUnion([Q0, Q1, Q2, Q3, Q4, Q5, Q6, Q7, Q8, Q9, Q10, Q11, Q12, Q13, Q14, Q15]), "operationType" : NewBodyOperationType.ADD, "depth" : 7 * mm, "offsetDistance" : 25 * mm});
        }
        {
            var Q0;
            Q0=makeQuery(id+"F1.opExtrude","CAP_FACE",FACE,{"disambiguationData":[OSD([sQuery(id+"F0.wireOp",EDGE,"E0"),sQuery(id+"F0.wireOp",EDGE,"E1"),sQuery(id+"F0.wireOp",EDGE,"E2"),sQuery(id+"F0.wireOp",EDGE,"E3"),sQuery(id+"F0.wireOp",EDGE,"E5"),sQuery(id+"F0.wireOp",EDGE,"E6"),sQuery(id+"F0.wireOp",EDGE,"E8"),sQuery(id+"F0.wireOp",EDGE,"E9"),sQuery(id+"F0.wireOp",EDGE,"E10"),sQuery(id+"F0.wireOp",EDGE,"E11"),sQuery(id+"F0.wireOp",EDGE,"E18"),sQuery(id+"F0.wireOp",EDGE,"E21"),sQuery(id+"F0.wireOp",EDGE,"E24"),sQuery(id+"F0.wireOp",EDGE,"E27"),sQuery(id+"F0.wireOp",EDGE,"E30"),sQuery(id+"F0.wireOp",EDGE,"E32"),sQuery(id+"F0.wireOp",EDGE,"E33"),sQuery(id+"F0.wireOp",EDGE,"E34"),sQuery(id+"F0.wireOp",EDGE,"E35"),sQuery(id+"F0.wireOp",EDGE,"E36"),sQuery(id+"F0.wireOp",EDGE,"E37"),sQuery(id+"F0.wireOp",EDGE,"E38"),sQuery(id+"F0.wireOp",EDGE,"E39"),sQuery(id+"F0.wireOp",EDGE,"E40"),sQuery(id+"F0.wireOp",EDGE,"E41"),sQuery(id+"F0.wireOp",EDGE,"E42"),sQuery(id+"F0.wireOp",EDGE,"E43"),sQuery(id+"F0.wireOp",EDGE,"E44.filletArc"),sQuery(id+"F0.wireOp",EDGE,"E45.filletArc"),sQuery(id+"F0.wireOp",EDGE,"E46.filletArc"),sQuery(id+"F0.wireOp",EDGE,"E47.filletArc"),sQuery(id+"F0.wireOp",EDGE,"E48.filletArc"),sQuery(id+"F0.wireOp",EDGE,"E49.filletArc"),sQuery(id+"F0.wireOp",EDGE,"E50.filletArc"),sQuery(id+"F0.wireOp",EDGE,"E51.filletArc"),sQuery(id+"F0.wireOp",EDGE,"E52"),sQuery(id+"F0.wireOp",EDGE,"E53"),sQuery(id+"F0.wireOp",EDGE,"E54"),sQuery(id+"F0.wireOp",EDGE,"E55"),sQuery(id+"F0.wireOp",EDGE,"E56"),sQuery(id+"F0.wireOp",EDGE,"E58"),sQuery(id+"F0.wireOp",EDGE,"E59"),sQuery(id+"F0.wireOp",EDGE,"E60.filletArc"),sQuery(id+"F0.wireOp",EDGE,"E61.filletArc"),sQuery(id+"F0.wireOp",EDGE,"E62.trimOffspring"),sQuery(id+"F0.wireOp",EDGE,"E63.filletArc"),sQuery(id+"F0.wireOp",EDGE,"E64.filletArc"),sQuery(id+"F0.wireOp",EDGE,"E65.filletArc"),sQuery(id+"F0.wireOp",EDGE,"E66.trimOffspring"),sQuery(id+"F0.wireOp",EDGE,"E67.filletArc"),sQuery(id+"F0.wireOp",EDGE,"E68.filletArc"),sQuery(id+"F0.wireOp",EDGE,"E69.filletArc"),sQuery(id+"F0.wireOp",EDGE,"E70"),sQuery(id+"F0.wireOp",EDGE,"E71"),sQuery(id+"F0.wireOp",EDGE,"E72"),sQuery(id+"F0.wireOp",EDGE,"E73"),sQuery(id+"F0.wireOp",EDGE,"E74"),sQuery(id+"F0.wireOp",EDGE,"E75"),sQuery(id+"F0.wireOp",EDGE,"E76"),sQuery(id+"F0.wireOp",EDGE,"E77"),sQuery(id+"F0.wireOp",EDGE,"E78"),sQuery(id+"F0.wireOp",EDGE,"E79"),sQuery(id+"F0.wireOp",EDGE,"E80"),sQuery(id+"F0.wireOp",EDGE,"E81"),sQuery(id+"F0.wireOp",EDGE,"E82.filletArc"),sQuery(id+"F0.wireOp",EDGE,"E83.filletArc"),sQuery(id+"F0.wireOp",EDGE,"E84.filletArc"),sQuery(id+"F0.wireOp",EDGE,"E85.filletArc"),sQuery(id+"F0.wireOp",EDGE,"E86.filletArc"),sQuery(id+"F0.wireOp",EDGE,"E87.filletArc"),sQuery(id+"F0.wireOp",EDGE,"E88.filletArc"),sQuery(id+"F0.wireOp",EDGE,"E89.filletArc"),sQuery(id+"F0.wireOp",EDGE,"E90"),sQuery(id+"F0.wireOp",EDGE,"E91"),sQuery(id+"F0.wireOp",EDGE,"E92"),sQuery(id+"F0.wireOp",EDGE,"E93"),sQuery(id+"F0.wireOp",EDGE,"E94"),sQuery(id+"F0.wireOp",EDGE,"E95"),sQuery(id+"F0.wireOp",EDGE,"E96"),sQuery(id+"F0.wireOp",EDGE,"E97.filletArc"),sQuery(id+"F0.wireOp",EDGE,"E98.filletArc"),sQuery(id+"F0.wireOp",EDGE,"E99.trimOffspring"),sQuery(id+"F0.wireOp",EDGE,"E100.filletArc"),sQuery(id+"F0.wireOp",EDGE,"E101.filletArc"),sQuery(id+"F0.wireOp",EDGE,"E102.filletArc"),sQuery(id+"F0.wireOp",EDGE,"E103.trimOffspring"),sQuery(id+"F0.wireOp",EDGE,"E104.filletArc"),sQuery(id+"F0.wireOp",EDGE,"E105.filletArc"),sQuery(id+"F0.wireOp",EDGE,"E106.filletArc"),sQuery(id+"F0.wireOp",EDGE,"E110"),sQuery(id+"F0.wireOp",EDGE,"E112"),sQuery(id+"F0.wireOp",EDGE,"E118"),sQuery(id+"F0.wireOp",EDGE,"E119"),sQuery(id+"F0.wireOp",EDGE,"E121"),sQuery(id+"F0.wireOp",EDGE,"E122"),sQuery(id+"F0.wireOp",EDGE,"E123"),sQuery(id+"F0.wireOp",EDGE,"E124")])],"isStart":false});
            var sketch = newSketch(context, id + "F5", { "sketchPlane" : qUnion([Q0])});
            skArc(sketch, "E137", {"start": v(25.18, -3.5) * mm, "mid": v(25.18, -7.75) * mm, "end": v(29.42, -7.75) * mm});
            skArc(sketch, "E138", {"start": v(35.75, -1.42) * mm, "mid": v(35.75, 2.82) * mm, "end": v(31.5, 2.82) * mm});
            skLineSegment(sketch, "E139", {"start": v(25.18, -3.5) * mm, "end": v(31.5, 2.82) * mm});
            skLineSegment(sketch, "E140", {"start": v(29.42, -7.75) * mm, "end": v(35.78, -1.39) * mm});
            skSolve(sketch);
        }
        {
            var Q0;
            {var subQ1=sQuery(id+"F5.wireOp",EDGE,"E137");Q0=makeQuery(id+"F5.imprint","IMPRINT",FACE,{"disambiguationData":[TD([[makeQuery(id+"F5.imprint","IMPRINT",EDGE,{"derivedFrom":subQ1}),1.0]])]});}
            extrude(context, id + "F6", {"entities" : qUnion([Q0]), "operationType" : NewBodyOperationType.REMOVE, "oppositeDirection" : true, "depth" : 1 * mm, "offsetDistance" : 25 * mm});
        }
        {
            var Q0;
            Q0=makeQuery(id+"F1.opExtrude","CAP_FACE",FACE,{"disambiguationData":[OSD([sQuery(id+"F0.wireOp",EDGE,"E0"),sQuery(id+"F0.wireOp",EDGE,"E1"),sQuery(id+"F0.wireOp",EDGE,"E2"),sQuery(id+"F0.wireOp",EDGE,"E3"),sQuery(id+"F0.wireOp",EDGE,"E5"),sQuery(id+"F0.wireOp",EDGE,"E6"),sQuery(id+"F0.wireOp",EDGE,"E8"),sQuery(id+"F0.wireOp",EDGE,"E9"),sQuery(id+"F0.wireOp",EDGE,"E10"),sQuery(id+"F0.wireOp",EDGE,"E11"),sQuery(id+"F0.wireOp",EDGE,"E18"),sQuery(id+"F0.wireOp",EDGE,"E21"),sQuery(id+"F0.wireOp",EDGE,"E24"),sQuery(id+"F0.wireOp",EDGE,"E27"),sQuery(id+"F0.wireOp",EDGE,"E30"),sQuery(id+"F0.wireOp",EDGE,"E32"),sQuery(id+"F0.wireOp",EDGE,"E33"),sQuery(id+"F0.wireOp",EDGE,"E34"),sQuery(id+"F0.wireOp",EDGE,"E35"),sQuery(id+"F0.wireOp",EDGE,"E36"),sQuery(id+"F0.wireOp",EDGE,"E37"),sQuery(id+"F0.wireOp",EDGE,"E38"),sQuery(id+"F0.wireOp",EDGE,"E39"),sQuery(id+"F0.wireOp",EDGE,"E40"),sQuery(id+"F0.wireOp",EDGE,"E41"),sQuery(id+"F0.wireOp",EDGE,"E42"),sQuery(id+"F0.wireOp",EDGE,"E43"),sQuery(id+"F0.wireOp",EDGE,"E44.filletArc"),sQuery(id+"F0.wireOp",EDGE,"E45.filletArc"),sQuery(id+"F0.wireOp",EDGE,"E46.filletArc"),sQuery(id+"F0.wireOp",EDGE,"E47.filletArc"),sQuery(id+"F0.wireOp",EDGE,"E48.filletArc"),sQuery(id+"F0.wireOp",EDGE,"E49.filletArc"),sQuery(id+"F0.wireOp",EDGE,"E50.filletArc"),sQuery(id+"F0.wireOp",EDGE,"E51.filletArc"),sQuery(id+"F0.wireOp",EDGE,"E52"),sQuery(id+"F0.wireOp",EDGE,"E53"),sQuery(id+"F0.wireOp",EDGE,"E54"),sQuery(id+"F0.wireOp",EDGE,"E55"),sQuery(id+"F0.wireOp",EDGE,"E56"),sQuery(id+"F0.wireOp",EDGE,"E58"),sQuery(id+"F0.wireOp",EDGE,"E59"),sQuery(id+"F0.wireOp",EDGE,"E60.filletArc"),sQuery(id+"F0.wireOp",EDGE,"E61.filletArc"),sQuery(id+"F0.wireOp",EDGE,"E62.trimOffspring"),sQuery(id+"F0.wireOp",EDGE,"E63.filletArc"),sQuery(id+"F0.wireOp",EDGE,"E64.filletArc"),sQuery(id+"F0.wireOp",EDGE,"E65.filletArc"),sQuery(id+"F0.wireOp",EDGE,"E66.trimOffspring"),sQuery(id+"F0.wireOp",EDGE,"E67.filletArc"),sQuery(id+"F0.wireOp",EDGE,"E68.filletArc"),sQuery(id+"F0.wireOp",EDGE,"E69.filletArc"),sQuery(id+"F0.wireOp",EDGE,"E70"),sQuery(id+"F0.wireOp",EDGE,"E71"),sQuery(id+"F0.wireOp",EDGE,"E72"),sQuery(id+"F0.wireOp",EDGE,"E73"),sQuery(id+"F0.wireOp",EDGE,"E74"),sQuery(id+"F0.wireOp",EDGE,"E75"),sQuery(id+"F0.wireOp",EDGE,"E76"),sQuery(id+"F0.wireOp",EDGE,"E77"),sQuery(id+"F0.wireOp",EDGE,"E78"),sQuery(id+"F0.wireOp",EDGE,"E79"),sQuery(id+"F0.wireOp",EDGE,"E80"),sQuery(id+"F0.wireOp",EDGE,"E81"),sQuery(id+"F0.wireOp",EDGE,"E82.filletArc"),sQuery(id+"F0.wireOp",EDGE,"E83.filletArc"),sQuery(id+"F0.wireOp",EDGE,"E84.filletArc"),sQuery(id+"F0.wireOp",EDGE,"E85.filletArc"),sQuery(id+"F0.wireOp",EDGE,"E86.filletArc"),sQuery(id+"F0.wireOp",EDGE,"E87.filletArc"),sQuery(id+"F0.wireOp",EDGE,"E88.filletArc"),sQuery(id+"F0.wireOp",EDGE,"E89.filletArc"),sQuery(id+"F0.wireOp",EDGE,"E90"),sQuery(id+"F0.wireOp",EDGE,"E91"),sQuery(id+"F0.wireOp",EDGE,"E92"),sQuery(id+"F0.wireOp",EDGE,"E93"),sQuery(id+"F0.wireOp",EDGE,"E94"),sQuery(id+"F0.wireOp",EDGE,"E95"),sQuery(id+"F0.wireOp",EDGE,"E96"),sQuery(id+"F0.wireOp",EDGE,"E97.filletArc"),sQuery(id+"F0.wireOp",EDGE,"E98.filletArc"),sQuery(id+"F0.wireOp",EDGE,"E99.trimOffspring"),sQuery(id+"F0.wireOp",EDGE,"E100.filletArc"),sQuery(id+"F0.wireOp",EDGE,"E101.filletArc"),sQuery(id+"F0.wireOp",EDGE,"E102.filletArc"),sQuery(id+"F0.wireOp",EDGE,"E103.trimOffspring"),sQuery(id+"F0.wireOp",EDGE,"E104.filletArc"),sQuery(id+"F0.wireOp",EDGE,"E105.filletArc"),sQuery(id+"F0.wireOp",EDGE,"E106.filletArc"),sQuery(id+"F0.wireOp",EDGE,"E110"),sQuery(id+"F0.wireOp",EDGE,"E112"),sQuery(id+"F0.wireOp",EDGE,"E118"),sQuery(id+"F0.wireOp",EDGE,"E119"),sQuery(id+"F0.wireOp",EDGE,"E121"),sQuery(id+"F0.wireOp",EDGE,"E122"),sQuery(id+"F0.wireOp",EDGE,"E123"),sQuery(id+"F0.wireOp",EDGE,"E124")])],"isStart":false});
            var sketch = newSketch(context, id + "F7", { "sketchPlane" : qUnion([Q0])});
            skArc(sketch, "E141", {"start": v(35.82, 5.86) * mm, "mid": v(36.8, 3.88) * mm, "end": v(38.78, 2.9) * mm});
            skArc(sketch, "E142", {"start": v(37.1, 1.2) * mm, "mid": v(36.1, 3.17) * mm, "end": v(34.13, 4.16) * mm});
            skArc(sketch, "E143", {"start": v(23.84, -6.13) * mm, "mid": v(24.83, -8.1) * mm, "end": v(26.8, -9.1) * mm});
            skArc(sketch, "E144", {"start": v(25.1, -10.78) * mm, "mid": v(24.12, -8.8) * mm, "end": v(22.15, -7.82) * mm});
            skLineSegment(sketch, "E145", {"start": v(38.08, 1.61) * mm, "end": v(37.52, 1.06) * mm});
            skLineSegment(sketch, "E146", {"start": v(38.08, 1.61) * mm, "end": v(38.93, 2.46) * mm});
            skLineSegment(sketch, "E147", {"start": v(26.1, -10.36) * mm, "end": v(26.94, -9.52) * mm});
            skLineSegment(sketch, "E148", {"start": v(26.1, -10.36) * mm, "end": v(25.54, -10.93) * mm});
            skLineSegment(sketch, "E149", {"start": v(23.4, -5.98) * mm, "end": v(22, -7.4) * mm});
            skLineSegment(sketch, "E150", {"start": v(35.4, 6) * mm, "end": v(33.99, 4.6) * mm});
            skPoint(sketch, "E151.visualSharp", {"position": v(33.6, 4.2) * mm});
            skArc(sketch, "E151.filletArc", {"start": v(33.99, 4.6) * mm, "mid": v(33.92, 4.33) * mm, "end": v(34.13, 4.16) * mm});
            skPoint(sketch, "E152.visualSharp", {"position": v(35.78, 6.4) * mm});
            skArc(sketch, "E152.filletArc", {"start": v(35.82, 5.86) * mm, "mid": v(35.65, 6.06) * mm, "end": v(35.4, 6) * mm});
            skPoint(sketch, "E153.visualSharp", {"position": v(37.13, 0.66) * mm});
            skArc(sketch, "E153.filletArc", {"start": v(37.1, 1.2) * mm, "mid": v(37.26, 1) * mm, "end": v(37.52, 1.06) * mm});
            skPoint(sketch, "E154.visualSharp", {"position": v(39.32, 2.86) * mm});
            skArc(sketch, "E154.filletArc", {"start": v(38.93, 2.46) * mm, "mid": v(38.99, 2.72) * mm, "end": v(38.78, 2.9) * mm});
            skPoint(sketch, "E155.visualSharp", {"position": v(21.6, -7.78) * mm});
            skArc(sketch, "E155.filletArc", {"start": v(22, -7.4) * mm, "mid": v(21.94, -7.65) * mm, "end": v(22.15, -7.82) * mm});
            skPoint(sketch, "E156.visualSharp", {"position": v(23.8, -5.6) * mm});
            skArc(sketch, "E156.filletArc", {"start": v(23.84, -6.13) * mm, "mid": v(23.67, -5.92) * mm, "end": v(23.4, -5.98) * mm});
            skPoint(sketch, "E157.visualSharp", {"position": v(25.14, -11.32) * mm});
            skArc(sketch, "E157.filletArc", {"start": v(25.1, -10.78) * mm, "mid": v(25.28, -10.99) * mm, "end": v(25.54, -10.93) * mm});
            skPoint(sketch, "E158.visualSharp", {"position": v(27.34, -9.13) * mm});
            skArc(sketch, "E158.filletArc", {"start": v(26.94, -9.52) * mm, "mid": v(27, -9.26) * mm, "end": v(26.8, -9.1) * mm});
            skSolve(sketch);
        }
        {
            var Q0;
            Q0 = qSketchRegion(id + "F7", true);
            extrude(context, id + "F8", {"entities" : qUnion([Q0]), "operationType" : NewBodyOperationType.REMOVE, "oppositeDirection" : true, "depth" : 1 * mm, "offsetDistance" : 25 * mm});
        }
        {
            var Q0;
            Q0=makeQuery(id+"F1.opExtrude","CAP_FACE",FACE,{"disambiguationData":[OSD([sQuery(id+"F0.wireOp",EDGE,"E0"),sQuery(id+"F0.wireOp",EDGE,"E1"),sQuery(id+"F0.wireOp",EDGE,"E2"),sQuery(id+"F0.wireOp",EDGE,"E3"),sQuery(id+"F0.wireOp",EDGE,"E5"),sQuery(id+"F0.wireOp",EDGE,"E6"),sQuery(id+"F0.wireOp",EDGE,"E8"),sQuery(id+"F0.wireOp",EDGE,"E9"),sQuery(id+"F0.wireOp",EDGE,"E10"),sQuery(id+"F0.wireOp",EDGE,"E11"),sQuery(id+"F0.wireOp",EDGE,"E18"),sQuery(id+"F0.wireOp",EDGE,"E21"),sQuery(id+"F0.wireOp",EDGE,"E24"),sQuery(id+"F0.wireOp",EDGE,"E27"),sQuery(id+"F0.wireOp",EDGE,"E30"),sQuery(id+"F0.wireOp",EDGE,"E32"),sQuery(id+"F0.wireOp",EDGE,"E33"),sQuery(id+"F0.wireOp",EDGE,"E34"),sQuery(id+"F0.wireOp",EDGE,"E35"),sQuery(id+"F0.wireOp",EDGE,"E36"),sQuery(id+"F0.wireOp",EDGE,"E37"),sQuery(id+"F0.wireOp",EDGE,"E38"),sQuery(id+"F0.wireOp",EDGE,"E39"),sQuery(id+"F0.wireOp",EDGE,"E40"),sQuery(id+"F0.wireOp",EDGE,"E41"),sQuery(id+"F0.wireOp",EDGE,"E42"),sQuery(id+"F0.wireOp",EDGE,"E43"),sQuery(id+"F0.wireOp",EDGE,"E44.filletArc"),sQuery(id+"F0.wireOp",EDGE,"E45.filletArc"),sQuery(id+"F0.wireOp",EDGE,"E46.filletArc"),sQuery(id+"F0.wireOp",EDGE,"E47.filletArc"),sQuery(id+"F0.wireOp",EDGE,"E48.filletArc"),sQuery(id+"F0.wireOp",EDGE,"E49.filletArc"),sQuery(id+"F0.wireOp",EDGE,"E50.filletArc"),sQuery(id+"F0.wireOp",EDGE,"E51.filletArc"),sQuery(id+"F0.wireOp",EDGE,"E52"),sQuery(id+"F0.wireOp",EDGE,"E53"),sQuery(id+"F0.wireOp",EDGE,"E54"),sQuery(id+"F0.wireOp",EDGE,"E55"),sQuery(id+"F0.wireOp",EDGE,"E56"),sQuery(id+"F0.wireOp",EDGE,"E58"),sQuery(id+"F0.wireOp",EDGE,"E59"),sQuery(id+"F0.wireOp",EDGE,"E60.filletArc"),sQuery(id+"F0.wireOp",EDGE,"E61.filletArc"),sQuery(id+"F0.wireOp",EDGE,"E62.trimOffspring"),sQuery(id+"F0.wireOp",EDGE,"E63.filletArc"),sQuery(id+"F0.wireOp",EDGE,"E64.filletArc"),sQuery(id+"F0.wireOp",EDGE,"E65.filletArc"),sQuery(id+"F0.wireOp",EDGE,"E66.trimOffspring"),sQuery(id+"F0.wireOp",EDGE,"E67.filletArc"),sQuery(id+"F0.wireOp",EDGE,"E68.filletArc"),sQuery(id+"F0.wireOp",EDGE,"E69.filletArc"),sQuery(id+"F0.wireOp",EDGE,"E70"),sQuery(id+"F0.wireOp",EDGE,"E71"),sQuery(id+"F0.wireOp",EDGE,"E72"),sQuery(id+"F0.wireOp",EDGE,"E73"),sQuery(id+"F0.wireOp",EDGE,"E74"),sQuery(id+"F0.wireOp",EDGE,"E75"),sQuery(id+"F0.wireOp",EDGE,"E76"),sQuery(id+"F0.wireOp",EDGE,"E77"),sQuery(id+"F0.wireOp",EDGE,"E78"),sQuery(id+"F0.wireOp",EDGE,"E79"),sQuery(id+"F0.wireOp",EDGE,"E80"),sQuery(id+"F0.wireOp",EDGE,"E81"),sQuery(id+"F0.wireOp",EDGE,"E82.filletArc"),sQuery(id+"F0.wireOp",EDGE,"E83.filletArc"),sQuery(id+"F0.wireOp",EDGE,"E84.filletArc"),sQuery(id+"F0.wireOp",EDGE,"E85.filletArc"),sQuery(id+"F0.wireOp",EDGE,"E86.filletArc"),sQuery(id+"F0.wireOp",EDGE,"E87.filletArc"),sQuery(id+"F0.wireOp",EDGE,"E88.filletArc"),sQuery(id+"F0.wireOp",EDGE,"E89.filletArc"),sQuery(id+"F0.wireOp",EDGE,"E90"),sQuery(id+"F0.wireOp",EDGE,"E91"),sQuery(id+"F0.wireOp",EDGE,"E92"),sQuery(id+"F0.wireOp",EDGE,"E93"),sQuery(id+"F0.wireOp",EDGE,"E94"),sQuery(id+"F0.wireOp",EDGE,"E95"),sQuery(id+"F0.wireOp",EDGE,"E96"),sQuery(id+"F0.wireOp",EDGE,"E97.filletArc"),sQuery(id+"F0.wireOp",EDGE,"E98.filletArc"),sQuery(id+"F0.wireOp",EDGE,"E99.trimOffspring"),sQuery(id+"F0.wireOp",EDGE,"E100.filletArc"),sQuery(id+"F0.wireOp",EDGE,"E101.filletArc"),sQuery(id+"F0.wireOp",EDGE,"E102.filletArc"),sQuery(id+"F0.wireOp",EDGE,"E103.trimOffspring"),sQuery(id+"F0.wireOp",EDGE,"E104.filletArc"),sQuery(id+"F0.wireOp",EDGE,"E105.filletArc"),sQuery(id+"F0.wireOp",EDGE,"E106.filletArc"),sQuery(id+"F0.wireOp",EDGE,"E110"),sQuery(id+"F0.wireOp",EDGE,"E112"),sQuery(id+"F0.wireOp",EDGE,"E118"),sQuery(id+"F0.wireOp",EDGE,"E119"),sQuery(id+"F0.wireOp",EDGE,"E121"),sQuery(id+"F0.wireOp",EDGE,"E122"),sQuery(id+"F0.wireOp",EDGE,"E123"),sQuery(id+"F0.wireOp",EDGE,"E124")])],"isStart":false});
            var sketch = newSketch(context, id + "F9", { "sketchPlane" : qUnion([Q0])});
            skArc(sketch, "E159", {"start": v(18.84, -9.19) * mm, "mid": v(18.14, -11.28) * mm, "end": v(18.84, -13.38) * mm});
            skArc(sketch, "E160", {"start": v(16.45, -13.38) * mm, "mid": v(17.14, -11.28) * mm, "end": v(16.45, -9.19) * mm});
            skLineSegment(sketch, "E161", {"start": v(17.62, -13.78) * mm, "end": v(16.65, -13.78) * mm});
            skLineSegment(sketch, "E162", {"start": v(17.62, -13.78) * mm, "end": v(18.64, -13.78) * mm});
            skLineSegment(sketch, "E163", {"start": v(18.64, -8.78) * mm, "end": v(16.65, -8.78) * mm});
            skPoint(sketch, "E164.visualSharp", {"position": v(16.1, -8.78) * mm});
            skArc(sketch, "E164.filletArc", {"start": v(16.65, -8.78) * mm, "mid": v(16.42, -8.92) * mm, "end": v(16.45, -9.19) * mm});
            skPoint(sketch, "E165.visualSharp", {"position": v(19.2, -8.78) * mm});
            skArc(sketch, "E165.filletArc", {"start": v(18.84, -9.19) * mm, "mid": v(18.86, -8.92) * mm, "end": v(18.64, -8.78) * mm});
            skPoint(sketch, "E166.visualSharp", {"position": v(19.2, -13.78) * mm});
            skArc(sketch, "E166.filletArc", {"start": v(18.64, -13.78) * mm, "mid": v(18.86, -13.64) * mm, "end": v(18.84, -13.38) * mm});
            skPoint(sketch, "E167.visualSharp", {"position": v(16.1, -13.78) * mm});
            skArc(sketch, "E167.filletArc", {"start": v(16.45, -13.38) * mm, "mid": v(16.42, -13.64) * mm, "end": v(16.65, -13.78) * mm});
            skSolve(sketch);
        }
        {
            var Q0;
            Q0 = qSketchRegion(id + "F9", true);
            extrude(context, id + "F10", {"entities" : qUnion([Q0]), "operationType" : NewBodyOperationType.REMOVE, "oppositeDirection" : true, "depth" : 1 * mm, "offsetDistance" : 25 * mm});
        }
        {
            var Q0;
            {var subQ0=sQuery(id+"F0.wireOp",EDGE,"E112");var subQ1=sQuery(id+"F0.wireOp",EDGE,"E110");var subQ2=sQuery(id+"F0.wireOp",EDGE,"E30");var subQ3=sQuery(id+"F0.wireOp",EDGE,"E27");var subQ4=sQuery(id+"F0.wireOp",EDGE,"E24");var subQ5=sQuery(id+"F0.wireOp",EDGE,"E21");var subQ6=sQuery(id+"F0.wireOp",EDGE,"E18");var subQ7=sQuery(id+"F0.wireOp",EDGE,"E5");Q0=makeQuery(id+"F4.boolean.opBoolean","MERGE",FACE,{"derivedFrom":[makeQuery(id+"F1.opExtrude","CAP_FACE",FACE,{"disambiguationData":[OSD([sQuery(id+"F0.wireOp",EDGE,"E0"),sQuery(id+"F0.wireOp",EDGE,"E1"),sQuery(id+"F0.wireOp",EDGE,"E2"),sQuery(id+"F0.wireOp",EDGE,"E3"),subQ7,sQuery(id+"F0.wireOp",EDGE,"E6"),sQuery(id+"F0.wireOp",EDGE,"E8"),sQuery(id+"F0.wireOp",EDGE,"E9"),sQuery(id+"F0.wireOp",EDGE,"E10"),sQuery(id+"F0.wireOp",EDGE,"E11"),subQ6,subQ5,subQ4,subQ3,subQ2,sQuery(id+"F0.wireOp",EDGE,"E32"),sQuery(id+"F0.wireOp",EDGE,"E33"),sQuery(id+"F0.wireOp",EDGE,"E34"),sQuery(id+"F0.wireOp",EDGE,"E35"),sQuery(id+"F0.wireOp",EDGE,"E36"),sQuery(id+"F0.wireOp",EDGE,"E37"),sQuery(id+"F0.wireOp",EDGE,"E38"),sQuery(id+"F0.wireOp",EDGE,"E39"),sQuery(id+"F0.wireOp",EDGE,"E40"),sQuery(id+"F0.wireOp",EDGE,"E41"),sQuery(id+"F0.wireOp",EDGE,"E42"),sQuery(id+"F0.wireOp",EDGE,"E43"),sQuery(id+"F0.wireOp",EDGE,"E44.filletArc"),sQuery(id+"F0.wireOp",EDGE,"E45.filletArc"),sQuery(id+"F0.wireOp",EDGE,"E46.filletArc"),sQuery(id+"F0.wireOp",EDGE,"E47.filletArc"),sQuery(id+"F0.wireOp",EDGE,"E48.filletArc"),sQuery(id+"F0.wireOp",EDGE,"E49.filletArc"),sQuery(id+"F0.wireOp",EDGE,"E50.filletArc"),sQuery(id+"F0.wireOp",EDGE,"E51.filletArc"),sQuery(id+"F0.wireOp",EDGE,"E52"),sQuery(id+"F0.wireOp",EDGE,"E53"),sQuery(id+"F0.wireOp",EDGE,"E54"),sQuery(id+"F0.wireOp",EDGE,"E55"),sQuery(id+"F0.wireOp",EDGE,"E56"),sQuery(id+"F0.wireOp",EDGE,"E58"),sQuery(id+"F0.wireOp",EDGE,"E59"),sQuery(id+"F0.wireOp",EDGE,"E60.filletArc"),sQuery(id+"F0.wireOp",EDGE,"E61.filletArc"),sQuery(id+"F0.wireOp",EDGE,"E62.trimOffspring"),sQuery(id+"F0.wireOp",EDGE,"E63.filletArc"),sQuery(id+"F0.wireOp",EDGE,"E64.filletArc"),sQuery(id+"F0.wireOp",EDGE,"E65.filletArc"),sQuery(id+"F0.wireOp",EDGE,"E66.trimOffspring"),sQuery(id+"F0.wireOp",EDGE,"E67.filletArc"),sQuery(id+"F0.wireOp",EDGE,"E68.filletArc"),sQuery(id+"F0.wireOp",EDGE,"E69.filletArc"),sQuery(id+"F0.wireOp",EDGE,"E70"),sQuery(id+"F0.wireOp",EDGE,"E71"),sQuery(id+"F0.wireOp",EDGE,"E72"),sQuery(id+"F0.wireOp",EDGE,"E73"),sQuery(id+"F0.wireOp",EDGE,"E74"),sQuery(id+"F0.wireOp",EDGE,"E75"),sQuery(id+"F0.wireOp",EDGE,"E76"),sQuery(id+"F0.wireOp",EDGE,"E77"),sQuery(id+"F0.wireOp",EDGE,"E78"),sQuery(id+"F0.wireOp",EDGE,"E79"),sQuery(id+"F0.wireOp",EDGE,"E80"),sQuery(id+"F0.wireOp",EDGE,"E81"),sQuery(id+"F0.wireOp",EDGE,"E82.filletArc"),sQuery(id+"F0.wireOp",EDGE,"E83.filletArc"),sQuery(id+"F0.wireOp",EDGE,"E84.filletArc"),sQuery(id+"F0.wireOp",EDGE,"E85.filletArc"),sQuery(id+"F0.wireOp",EDGE,"E86.filletArc"),sQuery(id+"F0.wireOp",EDGE,"E87.filletArc"),sQuery(id+"F0.wireOp",EDGE,"E88.filletArc"),sQuery(id+"F0.wireOp",EDGE,"E89.filletArc"),sQuery(id+"F0.wireOp",EDGE,"E90"),sQuery(id+"F0.wireOp",EDGE,"E91"),sQuery(id+"F0.wireOp",EDGE,"E92"),sQuery(id+"F0.wireOp",EDGE,"E93"),sQuery(id+"F0.wireOp",EDGE,"E94"),sQuery(id+"F0.wireOp",EDGE,"E95"),sQuery(id+"F0.wireOp",EDGE,"E96"),sQuery(id+"F0.wireOp",EDGE,"E97.filletArc"),sQuery(id+"F0.wireOp",EDGE,"E98.filletArc"),sQuery(id+"F0.wireOp",EDGE,"E99.trimOffspring"),sQuery(id+"F0.wireOp",EDGE,"E100.filletArc"),sQuery(id+"F0.wireOp",EDGE,"E101.filletArc"),sQuery(id+"F0.wireOp",EDGE,"E102.filletArc"),sQuery(id+"F0.wireOp",EDGE,"E103.trimOffspring"),sQuery(id+"F0.wireOp",EDGE,"E104.filletArc"),sQuery(id+"F0.wireOp",EDGE,"E105.filletArc"),sQuery(id+"F0.wireOp",EDGE,"E106.filletArc"),subQ1,subQ0,sQuery(id+"F0.wireOp",EDGE,"E118"),sQuery(id+"F0.wireOp",EDGE,"E119"),sQuery(id+"F0.wireOp",EDGE,"E121"),sQuery(id+"F0.wireOp",EDGE,"E122"),sQuery(id+"F0.wireOp",EDGE,"E123"),sQuery(id+"F0.wireOp",EDGE,"E124")])],"isStart":true}),makeQuery(id+"F4.opExtrude","CAP_FACE",FACE,{"disambiguationData":[OSD([sQuery(id+"F0.wireOp",EDGE,"E4"),subQ7])],"isStart":true}),makeQuery(id+"F4.opExtrude","CAP_FACE",FACE,{"disambiguationData":[OSD([sQuery(id+"F0.wireOp",EDGE,"E17"),subQ6])],"isStart":true}),makeQuery(id+"F4.opExtrude","CAP_FACE",FACE,{"disambiguationData":[OSD([sQuery(id+"F0.wireOp",EDGE,"E20"),subQ5])],"isStart":true}),makeQuery(id+"F4.opExtrude","CAP_FACE",FACE,{"disambiguationData":[OSD([sQuery(id+"F0.wireOp",EDGE,"E23"),subQ4])],"isStart":true}),makeQuery(id+"F4.opExtrude","CAP_FACE",FACE,{"disambiguationData":[OSD([sQuery(id+"F0.wireOp",EDGE,"E26"),subQ3])],"isStart":true}),makeQuery(id+"F4.opExtrude","CAP_FACE",FACE,{"disambiguationData":[OSD([sQuery(id+"F0.wireOp",EDGE,"E29"),subQ2])],"isStart":true}),makeQuery(id+"F4.opExtrude","CAP_FACE",FACE,{"disambiguationData":[OSD([subQ1,sQuery(id+"F0.wireOp",EDGE,"E111")])],"isStart":true}),makeQuery(id+"F4.opExtrude","CAP_FACE",FACE,{"disambiguationData":[OSD([subQ0,sQuery(id+"F0.wireOp",EDGE,"E113")])],"isStart":true})]});}
            extrude(context, id + "F11", {"entities" : qUnion([Q0]), "operationType" : NewBodyOperationType.REMOVE, "oppositeDirection" : true, "depth" : 4 * mm, "offsetDistance" : 25 * mm});
        }
        {
            var Q0;
            Q0=makeQuery(id+"F1.opExtrude","SWEPT_BODY",BODY,{"disambiguationData":[OSD([sQuery(id+"F0.wireOp",EDGE,"E0"),sQuery(id+"F0.wireOp",EDGE,"E1"),sQuery(id+"F0.wireOp",EDGE,"E2"),sQuery(id+"F0.wireOp",EDGE,"E3"),sQuery(id+"F0.wireOp",EDGE,"E5"),sQuery(id+"F0.wireOp",EDGE,"E6"),sQuery(id+"F0.wireOp",EDGE,"E8"),sQuery(id+"F0.wireOp",EDGE,"E9"),sQuery(id+"F0.wireOp",EDGE,"E10"),sQuery(id+"F0.wireOp",EDGE,"E11"),sQuery(id+"F0.wireOp",EDGE,"E18"),sQuery(id+"F0.wireOp",EDGE,"E21"),sQuery(id+"F0.wireOp",EDGE,"E24"),sQuery(id+"F0.wireOp",EDGE,"E27"),sQuery(id+"F0.wireOp",EDGE,"E30"),sQuery(id+"F0.wireOp",EDGE,"E32"),sQuery(id+"F0.wireOp",EDGE,"E33"),sQuery(id+"F0.wireOp",EDGE,"E34"),sQuery(id+"F0.wireOp",EDGE,"E35"),sQuery(id+"F0.wireOp",EDGE,"E36"),sQuery(id+"F0.wireOp",EDGE,"E37"),sQuery(id+"F0.wireOp",EDGE,"E38"),sQuery(id+"F0.wireOp",EDGE,"E39"),sQuery(id+"F0.wireOp",EDGE,"E40"),sQuery(id+"F0.wireOp",EDGE,"E41"),sQuery(id+"F0.wireOp",EDGE,"E42"),sQuery(id+"F0.wireOp",EDGE,"E43"),sQuery(id+"F0.wireOp",EDGE,"E44.filletArc"),sQuery(id+"F0.wireOp",EDGE,"E45.filletArc"),sQuery(id+"F0.wireOp",EDGE,"E46.filletArc"),sQuery(id+"F0.wireOp",EDGE,"E47.filletArc"),sQuery(id+"F0.wireOp",EDGE,"E48.filletArc"),sQuery(id+"F0.wireOp",EDGE,"E49.filletArc"),sQuery(id+"F0.wireOp",EDGE,"E50.filletArc"),sQuery(id+"F0.wireOp",EDGE,"E51.filletArc"),sQuery(id+"F0.wireOp",EDGE,"E52"),sQuery(id+"F0.wireOp",EDGE,"E53"),sQuery(id+"F0.wireOp",EDGE,"E54"),sQuery(id+"F0.wireOp",EDGE,"E55"),sQuery(id+"F0.wireOp",EDGE,"E56"),sQuery(id+"F0.wireOp",EDGE,"E58"),sQuery(id+"F0.wireOp",EDGE,"E59"),sQuery(id+"F0.wireOp",EDGE,"E60.filletArc"),sQuery(id+"F0.wireOp",EDGE,"E61.filletArc"),sQuery(id+"F0.wireOp",EDGE,"E62.trimOffspring"),sQuery(id+"F0.wireOp",EDGE,"E63.filletArc"),sQuery(id+"F0.wireOp",EDGE,"E64.filletArc"),sQuery(id+"F0.wireOp",EDGE,"E65.filletArc"),sQuery(id+"F0.wireOp",EDGE,"E66.trimOffspring"),sQuery(id+"F0.wireOp",EDGE,"E67.filletArc"),sQuery(id+"F0.wireOp",EDGE,"E68.filletArc"),sQuery(id+"F0.wireOp",EDGE,"E69.filletArc"),sQuery(id+"F0.wireOp",EDGE,"E70"),sQuery(id+"F0.wireOp",EDGE,"E71"),sQuery(id+"F0.wireOp",EDGE,"E72"),sQuery(id+"F0.wireOp",EDGE,"E73"),sQuery(id+"F0.wireOp",EDGE,"E74"),sQuery(id+"F0.wireOp",EDGE,"E75"),sQuery(id+"F0.wireOp",EDGE,"E76"),sQuery(id+"F0.wireOp",EDGE,"E77"),sQuery(id+"F0.wireOp",EDGE,"E78"),sQuery(id+"F0.wireOp",EDGE,"E79"),sQuery(id+"F0.wireOp",EDGE,"E80"),sQuery(id+"F0.wireOp",EDGE,"E81"),sQuery(id+"F0.wireOp",EDGE,"E82.filletArc"),sQuery(id+"F0.wireOp",EDGE,"E83.filletArc"),sQuery(id+"F0.wireOp",EDGE,"E84.filletArc"),sQuery(id+"F0.wireOp",EDGE,"E85.filletArc"),sQuery(id+"F0.wireOp",EDGE,"E86.filletArc"),sQuery(id+"F0.wireOp",EDGE,"E87.filletArc"),sQuery(id+"F0.wireOp",EDGE,"E88.filletArc"),sQuery(id+"F0.wireOp",EDGE,"E89.filletArc"),sQuery(id+"F0.wireOp",EDGE,"E90"),sQuery(id+"F0.wireOp",EDGE,"E91"),sQuery(id+"F0.wireOp",EDGE,"E92"),sQuery(id+"F0.wireOp",EDGE,"E93"),sQuery(id+"F0.wireOp",EDGE,"E94"),sQuery(id+"F0.wireOp",EDGE,"E95"),sQuery(id+"F0.wireOp",EDGE,"E96"),sQuery(id+"F0.wireOp",EDGE,"E97.filletArc"),sQuery(id+"F0.wireOp",EDGE,"E98.filletArc"),sQuery(id+"F0.wireOp",EDGE,"E99.trimOffspring"),sQuery(id+"F0.wireOp",EDGE,"E100.filletArc"),sQuery(id+"F0.wireOp",EDGE,"E101.filletArc"),sQuery(id+"F0.wireOp",EDGE,"E102.filletArc"),sQuery(id+"F0.wireOp",EDGE,"E103.trimOffspring"),sQuery(id+"F0.wireOp",EDGE,"E104.filletArc"),sQuery(id+"F0.wireOp",EDGE,"E105.filletArc"),sQuery(id+"F0.wireOp",EDGE,"E106.filletArc"),sQuery(id+"F0.wireOp",EDGE,"E110"),sQuery(id+"F0.wireOp",EDGE,"E112"),sQuery(id+"F0.wireOp",EDGE,"E118"),sQuery(id+"F0.wireOp",EDGE,"E119"),sQuery(id+"F0.wireOp",EDGE,"E121"),sQuery(id+"F0.wireOp",EDGE,"E122"),sQuery(id+"F0.wireOp",EDGE,"E123"),sQuery(id+"F0.wireOp",EDGE,"E124")])]});
            var Q1;
            Q1=makeQuery(id+"F11.boolean.opBoolean","COPY",FACE,{"derivedFrom":makeQuery(id+"F11.opExtrude","CAP_FACE",FACE,{"disambiguationData":[OSD([sQuery(id+"F0.wireOp",EDGE,"E0"),sQuery(id+"F0.wireOp",EDGE,"E1"),sQuery(id+"F0.wireOp",EDGE,"E2"),sQuery(id+"F0.wireOp",EDGE,"E3"),sQuery(id+"F0.wireOp",EDGE,"E4"),sQuery(id+"F0.wireOp",EDGE,"E5"),sQuery(id+"F0.wireOp",EDGE,"E6"),sQuery(id+"F0.wireOp",EDGE,"E8"),sQuery(id+"F0.wireOp",EDGE,"E9"),sQuery(id+"F0.wireOp",EDGE,"E10"),sQuery(id+"F0.wireOp",EDGE,"E11"),sQuery(id+"F0.wireOp",EDGE,"E17"),sQuery(id+"F0.wireOp",EDGE,"E18"),sQuery(id+"F0.wireOp",EDGE,"E20"),sQuery(id+"F0.wireOp",EDGE,"E21"),sQuery(id+"F0.wireOp",EDGE,"E23"),sQuery(id+"F0.wireOp",EDGE,"E24"),sQuery(id+"F0.wireOp",EDGE,"E26"),sQuery(id+"F0.wireOp",EDGE,"E27"),sQuery(id+"F0.wireOp",EDGE,"E29"),sQuery(id+"F0.wireOp",EDGE,"E30"),sQuery(id+"F0.wireOp",EDGE,"E32"),sQuery(id+"F0.wireOp",EDGE,"E33"),sQuery(id+"F0.wireOp",EDGE,"E34"),sQuery(id+"F0.wireOp",EDGE,"E35"),sQuery(id+"F0.wireOp",EDGE,"E36"),sQuery(id+"F0.wireOp",EDGE,"E37"),sQuery(id+"F0.wireOp",EDGE,"E38"),sQuery(id+"F0.wireOp",EDGE,"E39"),sQuery(id+"F0.wireOp",EDGE,"E40"),sQuery(id+"F0.wireOp",EDGE,"E41"),sQuery(id+"F0.wireOp",EDGE,"E42"),sQuery(id+"F0.wireOp",EDGE,"E43"),sQuery(id+"F0.wireOp",EDGE,"E44.filletArc"),sQuery(id+"F0.wireOp",EDGE,"E45.filletArc"),sQuery(id+"F0.wireOp",EDGE,"E46.filletArc"),sQuery(id+"F0.wireOp",EDGE,"E47.filletArc"),sQuery(id+"F0.wireOp",EDGE,"E48.filletArc"),sQuery(id+"F0.wireOp",EDGE,"E49.filletArc"),sQuery(id+"F0.wireOp",EDGE,"E50.filletArc"),sQuery(id+"F0.wireOp",EDGE,"E51.filletArc"),sQuery(id+"F0.wireOp",EDGE,"E52"),sQuery(id+"F0.wireOp",EDGE,"E53"),sQuery(id+"F0.wireOp",EDGE,"E54"),sQuery(id+"F0.wireOp",EDGE,"E55"),sQuery(id+"F0.wireOp",EDGE,"E56"),sQuery(id+"F0.wireOp",EDGE,"E58"),sQuery(id+"F0.wireOp",EDGE,"E59"),sQuery(id+"F0.wireOp",EDGE,"E60.filletArc"),sQuery(id+"F0.wireOp",EDGE,"E61.filletArc"),sQuery(id+"F0.wireOp",EDGE,"E62.trimOffspring"),sQuery(id+"F0.wireOp",EDGE,"E63.filletArc"),sQuery(id+"F0.wireOp",EDGE,"E64.filletArc"),sQuery(id+"F0.wireOp",EDGE,"E65.filletArc"),sQuery(id+"F0.wireOp",EDGE,"E66.trimOffspring"),sQuery(id+"F0.wireOp",EDGE,"E67.filletArc"),sQuery(id+"F0.wireOp",EDGE,"E68.filletArc"),sQuery(id+"F0.wireOp",EDGE,"E69.filletArc"),sQuery(id+"F0.wireOp",EDGE,"E70"),sQuery(id+"F0.wireOp",EDGE,"E71"),sQuery(id+"F0.wireOp",EDGE,"E72"),sQuery(id+"F0.wireOp",EDGE,"E73"),sQuery(id+"F0.wireOp",EDGE,"E74"),sQuery(id+"F0.wireOp",EDGE,"E75"),sQuery(id+"F0.wireOp",EDGE,"E76"),sQuery(id+"F0.wireOp",EDGE,"E77"),sQuery(id+"F0.wireOp",EDGE,"E78"),sQuery(id+"F0.wireOp",EDGE,"E79"),sQuery(id+"F0.wireOp",EDGE,"E80"),sQuery(id+"F0.wireOp",EDGE,"E81"),sQuery(id+"F0.wireOp",EDGE,"E82.filletArc"),sQuery(id+"F0.wireOp",EDGE,"E83.filletArc"),sQuery(id+"F0.wireOp",EDGE,"E84.filletArc"),sQuery(id+"F0.wireOp",EDGE,"E85.filletArc"),sQuery(id+"F0.wireOp",EDGE,"E86.filletArc"),sQuery(id+"F0.wireOp",EDGE,"E87.filletArc"),sQuery(id+"F0.wireOp",EDGE,"E88.filletArc"),sQuery(id+"F0.wireOp",EDGE,"E89.filletArc"),sQuery(id+"F0.wireOp",EDGE,"E90"),sQuery(id+"F0.wireOp",EDGE,"E91"),sQuery(id+"F0.wireOp",EDGE,"E92"),sQuery(id+"F0.wireOp",EDGE,"E93"),sQuery(id+"F0.wireOp",EDGE,"E94"),sQuery(id+"F0.wireOp",EDGE,"E95"),sQuery(id+"F0.wireOp",EDGE,"E96"),sQuery(id+"F0.wireOp",EDGE,"E97.filletArc"),sQuery(id+"F0.wireOp",EDGE,"E98.filletArc"),sQuery(id+"F0.wireOp",EDGE,"E99.trimOffspring"),sQuery(id+"F0.wireOp",EDGE,"E100.filletArc"),sQuery(id+"F0.wireOp",EDGE,"E101.filletArc"),sQuery(id+"F0.wireOp",EDGE,"E102.filletArc"),sQuery(id+"F0.wireOp",EDGE,"E103.trimOffspring"),sQuery(id+"F0.wireOp",EDGE,"E104.filletArc"),sQuery(id+"F0.wireOp",EDGE,"E105.filletArc"),sQuery(id+"F0.wireOp",EDGE,"E106.filletArc"),sQuery(id+"F0.wireOp",EDGE,"E110"),sQuery(id+"F0.wireOp",EDGE,"E111"),sQuery(id+"F0.wireOp",EDGE,"E112"),sQuery(id+"F0.wireOp",EDGE,"E113"),sQuery(id+"F0.wireOp",EDGE,"E118"),sQuery(id+"F0.wireOp",EDGE,"E119"),sQuery(id+"F0.wireOp",EDGE,"E121"),sQuery(id+"F0.wireOp",EDGE,"E122"),sQuery(id+"F0.wireOp",EDGE,"E123"),sQuery(id+"F0.wireOp",EDGE,"E124")])],"isStart":false})});
            mirror(context, id + "F12", {"operationType" : NewBodyOperationType.ADD, "entities" : qUnion([Q0]), "mirrorPlane" : qUnion([Q1])});
        }
    });
